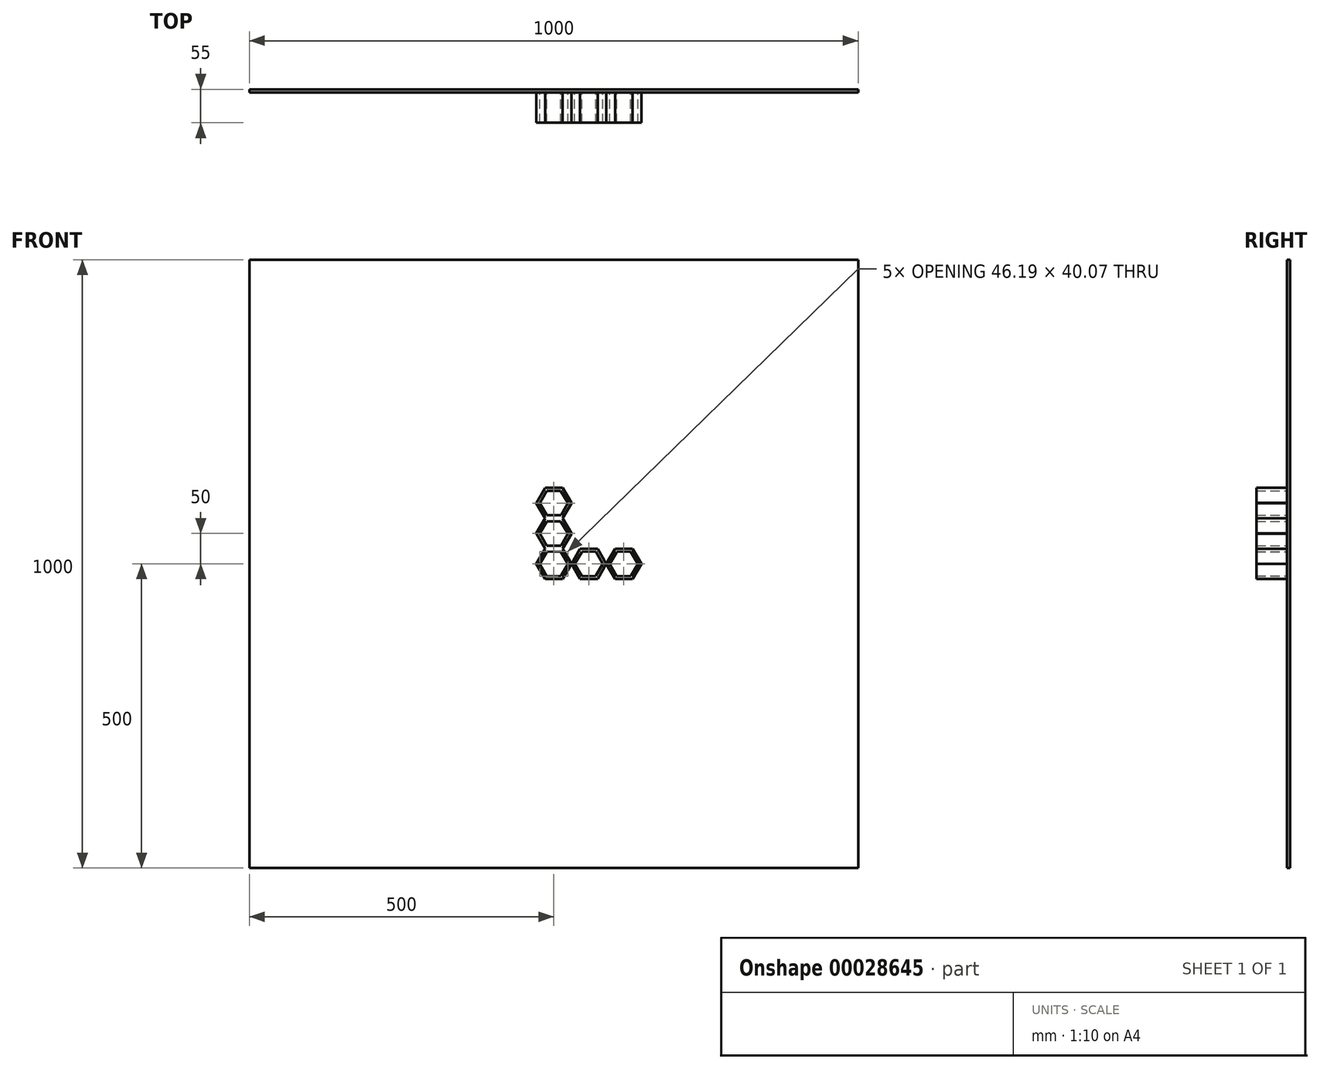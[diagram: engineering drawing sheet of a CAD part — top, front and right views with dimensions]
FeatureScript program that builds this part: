
annotation { "Feature Type Name" : "Feature", "Feature Type Description" : "" }
export const myFeature = defineFeature(function(context is Context, id is Id, definition is map)
    precondition{}
    {
        {
            var Q0;
            Q0=qCreatedBy(makeId("Front.planeOp"),FACE);
            var sketch = newSketch(context, id + "F0", { "sketchPlane" : qUnion([Q0])});
            skLineSegment(sketch, "E0.rect.bottom", {"start": v(500, 500) * mm, "end": v(-500, 500) * mm});
            skLineSegment(sketch, "E0.rect.top", {"start": v(500, -500) * mm, "end": v(-500, -500) * mm});
            skLineSegment(sketch, "E0.rect.left", {"start": v(500, 500) * mm, "end": v(500, -500) * mm});
            skLineSegment(sketch, "E0.rect.right", {"start": v(-500, 500) * mm, "end": v(-500, -500) * mm});
            skPoint(sketch, "E0.rect.middle", {"position": v(0, 0) * mm});
            skSolve(sketch);
        }
        {
            var Q0;
            Q0=makeQuery(id+"F0.imprint","IMPRINT",FACE,{"disambiguationData":[TD([[makeQuery(id+"F0.imprint","IMPRINT",EDGE,{"derivedFrom":sQuery(id+"F0.wireOp",EDGE,"E0.rect.bottom")}),1.0]])]});
            extrude(context, id + "F1", {"entities" : qUnion([Q0]), "depth" : 5 * mm});
        }
        {
            var Q0;
            Q0=makeQuery(id+"F1.opExtrude","CAP_FACE",FACE,{"disambiguationData":[OSD([sQuery(id+"F0.wireOp",EDGE,"E0.rect.bottom"),sQuery(id+"F0.wireOp",EDGE,"E0.rect.top"),sQuery(id+"F0.wireOp",EDGE,"E0.rect.left"),sQuery(id+"F0.wireOp",EDGE,"E0.rect.right")])],"isStart":false});
            var sketch = newSketch(context, id + "F2", { "sketchPlane" : qUnion([Q0])});
            skCircle(sketch, "E1.cCircle", {"center": v(0, 0) * mm, "radius": 25 * mm, "construction": true});
            skLineSegment(sketch, "E1.0", {"start": v(-14.43, 25) * mm, "end": v(14.43, 25) * mm});
            skLineSegment(sketch, "E1.1", {"start": v(14.43, 25) * mm, "end": v(28.87, 0) * mm});
            skLineSegment(sketch, "E1.2", {"start": v(28.87, 0) * mm, "end": v(14.43, -25) * mm});
            skLineSegment(sketch, "E1.3", {"start": v(14.43, -25) * mm, "end": v(-14.43, -25) * mm});
            skLineSegment(sketch, "E1.4", {"start": v(-14.43, -25) * mm, "end": v(-28.87, 0) * mm});
            skLineSegment(sketch, "E1.5", {"start": v(-28.87, 0) * mm, "end": v(-14.43, 25) * mm});
            skPoint(sketch, "E1.0.midPoint", {"position": v(0, 25) * mm});
            skCircle(sketch, "E2.cCircle", {"center": v(0, 0) * mm, "radius": 20 * mm, "construction": true});
            skLineSegment(sketch, "E2.0", {"start": v(11.49, 20.04) * mm, "end": v(23.1, 0.07) * mm});
            skLineSegment(sketch, "E2.1", {"start": v(23.1, 0.07) * mm, "end": v(11.6, -19.96) * mm});
            skLineSegment(sketch, "E2.2", {"start": v(11.6, -19.96) * mm, "end": v(-11.49, -20.04) * mm});
            skLineSegment(sketch, "E2.3", {"start": v(-11.49, -20.04) * mm, "end": v(-23.1, -0.07) * mm});
            skLineSegment(sketch, "E2.4", {"start": v(-23.1, -0.07) * mm, "end": v(-11.6, 19.96) * mm});
            skLineSegment(sketch, "E2.5", {"start": v(-11.6, 19.96) * mm, "end": v(11.49, 20.04) * mm});
            skPoint(sketch, "E2.0.midPoint", {"position": v(17.29, 10.05) * mm});
            skLineSegment(sketch, "E3.0.1.7", {"start": v(-14.43, 25) * mm, "end": v(-28.87, 50) * mm});
            skLineSegment(sketch, "E3.0.1.9", {"start": v(14.43, 25) * mm, "end": v(-14.43, 25) * mm});
            skLineSegment(sketch, "E3.0.1.10", {"start": v(28.87, 50) * mm, "end": v(14.43, 25) * mm});
            skPoint(sketch, "E3.0.1.12", {"position": v(0, 75) * mm});
            skPoint(sketch, "E3.0.1.13", {"position": v(17.29, 60.05) * mm});
            skLineSegment(sketch, "E3.0.1.16", {"start": v(11.6, 30.04) * mm, "end": v(-11.49, 29.96) * mm});
            skCircle(sketch, "E3.0.1.19", {"center": v(0, 50) * mm, "radius": 25 * mm, "construction": true});
            skLineSegment(sketch, "E3.0.1.20", {"start": v(-14.43, 75) * mm, "end": v(14.43, 75) * mm});
            skLineSegment(sketch, "E3.0.1.23", {"start": v(-11.6, 69.96) * mm, "end": v(11.49, 70.04) * mm});
            skLineSegment(sketch, "E3.0.1.28", {"start": v(-28.87, 50) * mm, "end": v(-14.43, 75) * mm});
            skLineSegment(sketch, "E3.0.1.31", {"start": v(14.43, 75) * mm, "end": v(28.87, 50) * mm});
            skCircle(sketch, "E3.0.1.36", {"center": v(0, 50) * mm, "radius": 20 * mm, "construction": true});
            skLineSegment(sketch, "E3.0.1.38", {"start": v(-23.1, 49.93) * mm, "end": v(-11.6, 69.96) * mm});
            skLineSegment(sketch, "E3.0.1.39", {"start": v(-11.49, 29.96) * mm, "end": v(-23.1, 49.93) * mm});
            skLineSegment(sketch, "E3.0.1.40", {"start": v(23.1, 50.07) * mm, "end": v(11.6, 30.04) * mm});
            skLineSegment(sketch, "E3.0.1.41", {"start": v(11.49, 70.04) * mm, "end": v(23.1, 50.07) * mm});
            skLineSegment(sketch, "E3.0.2.7", {"start": v(-14.43, 75) * mm, "end": v(-28.87, 100) * mm});
            skLineSegment(sketch, "E3.0.2.9", {"start": v(14.43, 75) * mm, "end": v(-14.43, 75) * mm});
            skLineSegment(sketch, "E3.0.2.10", {"start": v(28.87, 100) * mm, "end": v(14.43, 75) * mm});
            skPoint(sketch, "E3.0.2.12", {"position": v(0, 125) * mm});
            skPoint(sketch, "E3.0.2.13", {"position": v(17.29, 110.05) * mm});
            skLineSegment(sketch, "E3.0.2.16", {"start": v(11.6, 80.04) * mm, "end": v(-11.49, 79.96) * mm});
            skCircle(sketch, "E3.0.2.19", {"center": v(0, 100) * mm, "radius": 25 * mm, "construction": true});
            skLineSegment(sketch, "E3.0.2.20", {"start": v(-14.43, 125) * mm, "end": v(14.43, 125) * mm});
            skLineSegment(sketch, "E3.0.2.23", {"start": v(-11.6, 119.96) * mm, "end": v(11.49, 120.04) * mm});
            skLineSegment(sketch, "E3.0.2.28", {"start": v(-28.87, 100) * mm, "end": v(-14.43, 125) * mm});
            skLineSegment(sketch, "E3.0.2.31", {"start": v(14.43, 125) * mm, "end": v(28.87, 100) * mm});
            skCircle(sketch, "E3.0.2.36", {"center": v(0, 100) * mm, "radius": 20 * mm, "construction": true});
            skLineSegment(sketch, "E3.0.2.38", {"start": v(-23.1, 99.93) * mm, "end": v(-11.6, 119.96) * mm});
            skLineSegment(sketch, "E3.0.2.39", {"start": v(-11.49, 79.96) * mm, "end": v(-23.1, 99.93) * mm});
            skLineSegment(sketch, "E3.0.2.40", {"start": v(23.1, 100.07) * mm, "end": v(11.6, 80.04) * mm});
            skLineSegment(sketch, "E3.0.2.41", {"start": v(11.49, 120.04) * mm, "end": v(23.1, 100.07) * mm});
            skLineSegment(sketch, "E3.0.3.7", {"start": v(-14.43, 125) * mm, "end": v(-28.87, 150) * mm});
            skLineSegment(sketch, "E3.0.3.9", {"start": v(14.43, 125) * mm, "end": v(-14.43, 125) * mm});
            skLineSegment(sketch, "E3.0.3.10", {"start": v(28.87, 150) * mm, "end": v(14.43, 125) * mm});
            skPoint(sketch, "E3.0.3.12", {"position": v(0, 175) * mm});
            skPoint(sketch, "E3.0.3.13", {"position": v(17.29, 160.05) * mm});
            skLineSegment(sketch, "E3.0.3.16", {"start": v(11.6, 130.04) * mm, "end": v(-11.49, 129.96) * mm});
            skCircle(sketch, "E3.0.3.19", {"center": v(0, 150) * mm, "radius": 25 * mm, "construction": true});
            skLineSegment(sketch, "E3.0.3.20", {"start": v(-14.43, 175) * mm, "end": v(14.43, 175) * mm});
            skLineSegment(sketch, "E3.0.3.23", {"start": v(-11.6, 169.96) * mm, "end": v(11.49, 170.04) * mm});
            skLineSegment(sketch, "E3.0.3.28", {"start": v(-28.87, 150) * mm, "end": v(-14.43, 175) * mm});
            skLineSegment(sketch, "E3.0.3.31", {"start": v(14.43, 175) * mm, "end": v(28.87, 150) * mm});
            skCircle(sketch, "E3.0.3.36", {"center": v(0, 150) * mm, "radius": 20 * mm, "construction": true});
            skLineSegment(sketch, "E3.0.3.38", {"start": v(-23.1, 149.93) * mm, "end": v(-11.6, 169.96) * mm});
            skLineSegment(sketch, "E3.0.3.39", {"start": v(-11.49, 129.96) * mm, "end": v(-23.1, 149.93) * mm});
            skLineSegment(sketch, "E3.0.3.40", {"start": v(23.1, 150.07) * mm, "end": v(11.6, 130.04) * mm});
            skLineSegment(sketch, "E3.0.3.41", {"start": v(11.49, 170.04) * mm, "end": v(23.1, 150.07) * mm});
            skLineSegment(sketch, "E3.0.4.7", {"start": v(-14.43, 175) * mm, "end": v(-28.87, 200) * mm});
            skLineSegment(sketch, "E3.0.4.9", {"start": v(14.43, 175) * mm, "end": v(-14.43, 175) * mm});
            skLineSegment(sketch, "E3.0.4.10", {"start": v(28.87, 200) * mm, "end": v(14.43, 175) * mm});
            skPoint(sketch, "E3.0.4.12", {"position": v(0, 225) * mm});
            skPoint(sketch, "E3.0.4.13", {"position": v(17.29, 210.05) * mm});
            skLineSegment(sketch, "E3.0.4.16", {"start": v(11.6, 180.04) * mm, "end": v(-11.49, 179.96) * mm});
            skCircle(sketch, "E3.0.4.19", {"center": v(0, 200) * mm, "radius": 25 * mm, "construction": true});
            skLineSegment(sketch, "E3.0.4.20", {"start": v(-14.43, 225) * mm, "end": v(14.43, 225) * mm});
            skLineSegment(sketch, "E3.0.4.23", {"start": v(-11.6, 219.96) * mm, "end": v(11.49, 220.04) * mm});
            skLineSegment(sketch, "E3.0.4.28", {"start": v(-28.87, 200) * mm, "end": v(-14.43, 225) * mm});
            skLineSegment(sketch, "E3.0.4.31", {"start": v(14.43, 225) * mm, "end": v(28.87, 200) * mm});
            skCircle(sketch, "E3.0.4.36", {"center": v(0, 200) * mm, "radius": 20 * mm, "construction": true});
            skLineSegment(sketch, "E3.0.4.38", {"start": v(-23.1, 199.93) * mm, "end": v(-11.6, 219.96) * mm});
            skLineSegment(sketch, "E3.0.4.39", {"start": v(-11.49, 179.96) * mm, "end": v(-23.1, 199.93) * mm});
            skLineSegment(sketch, "E3.0.4.40", {"start": v(23.1, 200.07) * mm, "end": v(11.6, 180.04) * mm});
            skLineSegment(sketch, "E3.0.4.41", {"start": v(11.49, 220.04) * mm, "end": v(23.1, 200.07) * mm});
            skLineSegment(sketch, "E3.0.5.7", {"start": v(-14.43, 225) * mm, "end": v(-28.87, 250) * mm});
            skLineSegment(sketch, "E3.0.5.9", {"start": v(14.43, 225) * mm, "end": v(-14.43, 225) * mm});
            skLineSegment(sketch, "E3.0.5.10", {"start": v(28.87, 250) * mm, "end": v(14.43, 225) * mm});
            skPoint(sketch, "E3.0.5.12", {"position": v(0, 275) * mm});
            skPoint(sketch, "E3.0.5.13", {"position": v(17.29, 260.05) * mm});
            skLineSegment(sketch, "E3.0.5.16", {"start": v(11.6, 230.04) * mm, "end": v(-11.49, 229.96) * mm});
            skCircle(sketch, "E3.0.5.19", {"center": v(0, 250) * mm, "radius": 25 * mm, "construction": true});
            skLineSegment(sketch, "E3.0.5.20", {"start": v(-14.43, 275) * mm, "end": v(14.43, 275) * mm});
            skLineSegment(sketch, "E3.0.5.23", {"start": v(-11.6, 269.96) * mm, "end": v(11.49, 270.04) * mm});
            skLineSegment(sketch, "E3.0.5.28", {"start": v(-28.87, 250) * mm, "end": v(-14.43, 275) * mm});
            skLineSegment(sketch, "E3.0.5.31", {"start": v(14.43, 275) * mm, "end": v(28.87, 250) * mm});
            skCircle(sketch, "E3.0.5.36", {"center": v(0, 250) * mm, "radius": 20 * mm, "construction": true});
            skLineSegment(sketch, "E3.0.5.38", {"start": v(-23.1, 249.93) * mm, "end": v(-11.6, 269.96) * mm});
            skLineSegment(sketch, "E3.0.5.39", {"start": v(-11.49, 229.96) * mm, "end": v(-23.1, 249.93) * mm});
            skLineSegment(sketch, "E3.0.5.40", {"start": v(23.1, 250.07) * mm, "end": v(11.6, 230.04) * mm});
            skLineSegment(sketch, "E3.0.5.41", {"start": v(11.49, 270.04) * mm, "end": v(23.1, 250.07) * mm});
            skLineSegment(sketch, "E3.0.6.7", {"start": v(-14.43, 275) * mm, "end": v(-28.87, 300) * mm});
            skLineSegment(sketch, "E3.0.6.9", {"start": v(14.43, 275) * mm, "end": v(-14.43, 275) * mm});
            skLineSegment(sketch, "E3.0.6.10", {"start": v(28.87, 300) * mm, "end": v(14.43, 275) * mm});
            skPoint(sketch, "E3.0.6.12", {"position": v(0, 325) * mm});
            skPoint(sketch, "E3.0.6.13", {"position": v(17.29, 310.05) * mm});
            skLineSegment(sketch, "E3.0.6.16", {"start": v(11.6, 280.04) * mm, "end": v(-11.49, 279.96) * mm});
            skCircle(sketch, "E3.0.6.19", {"center": v(0, 300) * mm, "radius": 25 * mm, "construction": true});
            skLineSegment(sketch, "E3.0.6.20", {"start": v(-14.43, 325) * mm, "end": v(14.43, 325) * mm});
            skLineSegment(sketch, "E3.0.6.23", {"start": v(-11.6, 319.96) * mm, "end": v(11.49, 320.04) * mm});
            skLineSegment(sketch, "E3.0.6.28", {"start": v(-28.87, 300) * mm, "end": v(-14.43, 325) * mm});
            skLineSegment(sketch, "E3.0.6.31", {"start": v(14.43, 325) * mm, "end": v(28.87, 300) * mm});
            skCircle(sketch, "E3.0.6.36", {"center": v(0, 300) * mm, "radius": 20 * mm, "construction": true});
            skLineSegment(sketch, "E3.0.6.38", {"start": v(-23.1, 299.93) * mm, "end": v(-11.6, 319.96) * mm});
            skLineSegment(sketch, "E3.0.6.39", {"start": v(-11.49, 279.96) * mm, "end": v(-23.1, 299.93) * mm});
            skLineSegment(sketch, "E3.0.6.40", {"start": v(23.1, 300.07) * mm, "end": v(11.6, 280.04) * mm});
            skLineSegment(sketch, "E3.0.6.41", {"start": v(11.49, 320.04) * mm, "end": v(23.1, 300.07) * mm});
            skLineSegment(sketch, "E3.0.7.7", {"start": v(-14.43, 325) * mm, "end": v(-28.87, 350) * mm});
            skLineSegment(sketch, "E3.0.7.9", {"start": v(14.43, 325) * mm, "end": v(-14.43, 325) * mm});
            skLineSegment(sketch, "E3.0.7.10", {"start": v(28.87, 350) * mm, "end": v(14.43, 325) * mm});
            skPoint(sketch, "E3.0.7.12", {"position": v(0, 375) * mm});
            skPoint(sketch, "E3.0.7.13", {"position": v(17.29, 360.05) * mm});
            skLineSegment(sketch, "E3.0.7.16", {"start": v(11.6, 330.04) * mm, "end": v(-11.49, 329.96) * mm});
            skCircle(sketch, "E3.0.7.19", {"center": v(0, 350) * mm, "radius": 25 * mm, "construction": true});
            skLineSegment(sketch, "E3.0.7.20", {"start": v(-14.43, 375) * mm, "end": v(14.43, 375) * mm});
            skLineSegment(sketch, "E3.0.7.23", {"start": v(-11.6, 369.96) * mm, "end": v(11.49, 370.04) * mm});
            skLineSegment(sketch, "E3.0.7.28", {"start": v(-28.87, 350) * mm, "end": v(-14.43, 375) * mm});
            skLineSegment(sketch, "E3.0.7.31", {"start": v(14.43, 375) * mm, "end": v(28.87, 350) * mm});
            skCircle(sketch, "E3.0.7.36", {"center": v(0, 350) * mm, "radius": 20 * mm, "construction": true});
            skLineSegment(sketch, "E3.0.7.38", {"start": v(-23.1, 349.93) * mm, "end": v(-11.6, 369.96) * mm});
            skLineSegment(sketch, "E3.0.7.39", {"start": v(-11.49, 329.96) * mm, "end": v(-23.1, 349.93) * mm});
            skLineSegment(sketch, "E3.0.7.40", {"start": v(23.1, 350.07) * mm, "end": v(11.6, 330.04) * mm});
            skLineSegment(sketch, "E3.0.7.41", {"start": v(11.49, 370.04) * mm, "end": v(23.1, 350.07) * mm});
            skLineSegment(sketch, "E3.0.8.7", {"start": v(-14.43, 375) * mm, "end": v(-28.87, 400) * mm});
            skLineSegment(sketch, "E3.0.8.9", {"start": v(14.43, 375) * mm, "end": v(-14.43, 375) * mm});
            skLineSegment(sketch, "E3.0.8.10", {"start": v(28.87, 400) * mm, "end": v(14.43, 375) * mm});
            skPoint(sketch, "E3.0.8.12", {"position": v(0, 425) * mm});
            skPoint(sketch, "E3.0.8.13", {"position": v(17.29, 410.05) * mm});
            skLineSegment(sketch, "E3.0.8.16", {"start": v(11.6, 380.04) * mm, "end": v(-11.49, 379.96) * mm});
            skCircle(sketch, "E3.0.8.19", {"center": v(0, 400) * mm, "radius": 25 * mm, "construction": true});
            skLineSegment(sketch, "E3.0.8.20", {"start": v(-14.43, 425) * mm, "end": v(14.43, 425) * mm});
            skLineSegment(sketch, "E3.0.8.23", {"start": v(-11.6, 419.96) * mm, "end": v(11.49, 420.04) * mm});
            skLineSegment(sketch, "E3.0.8.28", {"start": v(-28.87, 400) * mm, "end": v(-14.43, 425) * mm});
            skLineSegment(sketch, "E3.0.8.31", {"start": v(14.43, 425) * mm, "end": v(28.87, 400) * mm});
            skCircle(sketch, "E3.0.8.36", {"center": v(0, 400) * mm, "radius": 20 * mm, "construction": true});
            skLineSegment(sketch, "E3.0.8.38", {"start": v(-23.1, 399.93) * mm, "end": v(-11.6, 419.96) * mm});
            skLineSegment(sketch, "E3.0.8.39", {"start": v(-11.49, 379.96) * mm, "end": v(-23.1, 399.93) * mm});
            skLineSegment(sketch, "E3.0.8.40", {"start": v(23.1, 400.07) * mm, "end": v(11.6, 380.04) * mm});
            skLineSegment(sketch, "E3.0.8.41", {"start": v(11.49, 420.04) * mm, "end": v(23.1, 400.07) * mm});
            skLineSegment(sketch, "E3.0.9.7", {"start": v(-14.43, 425) * mm, "end": v(-28.87, 450) * mm});
            skLineSegment(sketch, "E3.0.9.9", {"start": v(14.43, 425) * mm, "end": v(-14.43, 425) * mm});
            skLineSegment(sketch, "E3.0.9.10", {"start": v(28.87, 450) * mm, "end": v(14.43, 425) * mm});
            skPoint(sketch, "E3.0.9.12", {"position": v(0, 475) * mm});
            skPoint(sketch, "E3.0.9.13", {"position": v(17.29, 460.05) * mm});
            skLineSegment(sketch, "E3.0.9.16", {"start": v(11.6, 430.04) * mm, "end": v(-11.49, 429.96) * mm});
            skCircle(sketch, "E3.0.9.19", {"center": v(0, 450) * mm, "radius": 25 * mm, "construction": true});
            skLineSegment(sketch, "E3.0.9.20", {"start": v(-14.43, 475) * mm, "end": v(14.43, 475) * mm});
            skLineSegment(sketch, "E3.0.9.23", {"start": v(-11.6, 469.96) * mm, "end": v(11.49, 470.04) * mm});
            skLineSegment(sketch, "E3.0.9.28", {"start": v(-28.87, 450) * mm, "end": v(-14.43, 475) * mm});
            skLineSegment(sketch, "E3.0.9.31", {"start": v(14.43, 475) * mm, "end": v(28.87, 450) * mm});
            skCircle(sketch, "E3.0.9.36", {"center": v(0, 450) * mm, "radius": 20 * mm, "construction": true});
            skLineSegment(sketch, "E3.0.9.38", {"start": v(-23.1, 449.93) * mm, "end": v(-11.6, 469.96) * mm});
            skLineSegment(sketch, "E3.0.9.39", {"start": v(-11.49, 429.96) * mm, "end": v(-23.1, 449.93) * mm});
            skLineSegment(sketch, "E3.0.9.40", {"start": v(23.1, 450.07) * mm, "end": v(11.6, 430.04) * mm});
            skLineSegment(sketch, "E3.0.9.41", {"start": v(11.49, 470.04) * mm, "end": v(23.1, 450.07) * mm});
            skLineSegment(sketch, "E3.1.0.7", {"start": v(43.07, -25) * mm, "end": v(28.63, 0) * mm});
            skLineSegment(sketch, "E3.1.0.9", {"start": v(71.93, -25) * mm, "end": v(43.07, -25) * mm});
            skLineSegment(sketch, "E3.1.0.10", {"start": v(86.37, 0) * mm, "end": v(71.93, -25) * mm});
            skPoint(sketch, "E3.1.0.12", {"position": v(57.5, 25) * mm});
            skPoint(sketch, "E3.1.0.13", {"position": v(74.79, 10.05) * mm});
            skLineSegment(sketch, "E3.1.0.16", {"start": v(69.1, -19.96) * mm, "end": v(46.01, -20.04) * mm});
            skCircle(sketch, "E3.1.0.19", {"center": v(57.5, 0) * mm, "radius": 25 * mm, "construction": true});
            skLineSegment(sketch, "E3.1.0.20", {"start": v(43.07, 25) * mm, "end": v(71.93, 25) * mm});
            skLineSegment(sketch, "E3.1.0.23", {"start": v(45.9, 19.96) * mm, "end": v(68.99, 20.04) * mm});
            skLineSegment(sketch, "E3.1.0.28", {"start": v(28.63, 0) * mm, "end": v(43.07, 25) * mm});
            skLineSegment(sketch, "E3.1.0.31", {"start": v(71.93, 25) * mm, "end": v(86.37, 0) * mm});
            skCircle(sketch, "E3.1.0.36", {"center": v(57.5, 0) * mm, "radius": 20 * mm, "construction": true});
            skLineSegment(sketch, "E3.1.0.38", {"start": v(34.4, -0.07) * mm, "end": v(45.9, 19.96) * mm});
            skLineSegment(sketch, "E3.1.0.39", {"start": v(46.01, -20.04) * mm, "end": v(34.4, -0.07) * mm});
            skLineSegment(sketch, "E3.1.0.40", {"start": v(80.6, 0.07) * mm, "end": v(69.1, -19.96) * mm});
            skLineSegment(sketch, "E3.1.0.41", {"start": v(68.99, 20.04) * mm, "end": v(80.6, 0.07) * mm});
            skLineSegment(sketch, "E3.1.1.7", {"start": v(43.07, 25) * mm, "end": v(28.63, 50) * mm});
            skLineSegment(sketch, "E3.1.1.9", {"start": v(71.93, 25) * mm, "end": v(43.07, 25) * mm});
            skLineSegment(sketch, "E3.1.1.10", {"start": v(86.37, 50) * mm, "end": v(71.93, 25) * mm});
            skPoint(sketch, "E3.1.1.12", {"position": v(57.5, 75) * mm});
            skPoint(sketch, "E3.1.1.13", {"position": v(74.79, 60.05) * mm});
            skLineSegment(sketch, "E3.1.1.16", {"start": v(69.1, 30.04) * mm, "end": v(46.01, 29.96) * mm});
            skCircle(sketch, "E3.1.1.19", {"center": v(57.5, 50) * mm, "radius": 25 * mm, "construction": true});
            skLineSegment(sketch, "E3.1.1.20", {"start": v(43.07, 75) * mm, "end": v(71.93, 75) * mm});
            skLineSegment(sketch, "E3.1.1.23", {"start": v(45.9, 69.96) * mm, "end": v(68.99, 70.04) * mm});
            skLineSegment(sketch, "E3.1.1.28", {"start": v(28.63, 50) * mm, "end": v(43.07, 75) * mm});
            skLineSegment(sketch, "E3.1.1.31", {"start": v(71.93, 75) * mm, "end": v(86.37, 50) * mm});
            skCircle(sketch, "E3.1.1.36", {"center": v(57.5, 50) * mm, "radius": 20 * mm, "construction": true});
            skLineSegment(sketch, "E3.1.1.38", {"start": v(34.4, 49.93) * mm, "end": v(45.9, 69.96) * mm});
            skLineSegment(sketch, "E3.1.1.39", {"start": v(46.01, 29.96) * mm, "end": v(34.4, 49.93) * mm});
            skLineSegment(sketch, "E3.1.1.40", {"start": v(80.6, 50.07) * mm, "end": v(69.1, 30.04) * mm});
            skLineSegment(sketch, "E3.1.1.41", {"start": v(68.99, 70.04) * mm, "end": v(80.6, 50.07) * mm});
            skLineSegment(sketch, "E3.1.2.7", {"start": v(43.07, 75) * mm, "end": v(28.63, 100) * mm});
            skLineSegment(sketch, "E3.1.2.9", {"start": v(71.93, 75) * mm, "end": v(43.07, 75) * mm});
            skLineSegment(sketch, "E3.1.2.10", {"start": v(86.37, 100) * mm, "end": v(71.93, 75) * mm});
            skPoint(sketch, "E3.1.2.12", {"position": v(57.5, 125) * mm});
            skPoint(sketch, "E3.1.2.13", {"position": v(74.79, 110.05) * mm});
            skLineSegment(sketch, "E3.1.2.16", {"start": v(69.1, 80.04) * mm, "end": v(46.01, 79.96) * mm});
            skCircle(sketch, "E3.1.2.19", {"center": v(57.5, 100) * mm, "radius": 25 * mm, "construction": true});
            skLineSegment(sketch, "E3.1.2.20", {"start": v(43.07, 125) * mm, "end": v(71.93, 125) * mm});
            skLineSegment(sketch, "E3.1.2.23", {"start": v(45.9, 119.96) * mm, "end": v(68.99, 120.04) * mm});
            skLineSegment(sketch, "E3.1.2.28", {"start": v(28.63, 100) * mm, "end": v(43.07, 125) * mm});
            skLineSegment(sketch, "E3.1.2.31", {"start": v(71.93, 125) * mm, "end": v(86.37, 100) * mm});
            skCircle(sketch, "E3.1.2.36", {"center": v(57.5, 100) * mm, "radius": 20 * mm, "construction": true});
            skLineSegment(sketch, "E3.1.2.38", {"start": v(34.4, 99.93) * mm, "end": v(45.9, 119.96) * mm});
            skLineSegment(sketch, "E3.1.2.39", {"start": v(46.01, 79.96) * mm, "end": v(34.4, 99.93) * mm});
            skLineSegment(sketch, "E3.1.2.40", {"start": v(80.6, 100.07) * mm, "end": v(69.1, 80.04) * mm});
            skLineSegment(sketch, "E3.1.2.41", {"start": v(68.99, 120.04) * mm, "end": v(80.6, 100.07) * mm});
            skLineSegment(sketch, "E3.1.3.7", {"start": v(43.07, 125) * mm, "end": v(28.63, 150) * mm});
            skLineSegment(sketch, "E3.1.3.9", {"start": v(71.93, 125) * mm, "end": v(43.07, 125) * mm});
            skLineSegment(sketch, "E3.1.3.10", {"start": v(86.37, 150) * mm, "end": v(71.93, 125) * mm});
            skPoint(sketch, "E3.1.3.12", {"position": v(57.5, 175) * mm});
            skPoint(sketch, "E3.1.3.13", {"position": v(74.79, 160.05) * mm});
            skLineSegment(sketch, "E3.1.3.16", {"start": v(69.1, 130.04) * mm, "end": v(46.01, 129.96) * mm});
            skCircle(sketch, "E3.1.3.19", {"center": v(57.5, 150) * mm, "radius": 25 * mm, "construction": true});
            skLineSegment(sketch, "E3.1.3.20", {"start": v(43.07, 175) * mm, "end": v(71.93, 175) * mm});
            skLineSegment(sketch, "E3.1.3.23", {"start": v(45.9, 169.96) * mm, "end": v(68.99, 170.04) * mm});
            skLineSegment(sketch, "E3.1.3.28", {"start": v(28.63, 150) * mm, "end": v(43.07, 175) * mm});
            skLineSegment(sketch, "E3.1.3.31", {"start": v(71.93, 175) * mm, "end": v(86.37, 150) * mm});
            skCircle(sketch, "E3.1.3.36", {"center": v(57.5, 150) * mm, "radius": 20 * mm, "construction": true});
            skLineSegment(sketch, "E3.1.3.38", {"start": v(34.4, 149.93) * mm, "end": v(45.9, 169.96) * mm});
            skLineSegment(sketch, "E3.1.3.39", {"start": v(46.01, 129.96) * mm, "end": v(34.4, 149.93) * mm});
            skLineSegment(sketch, "E3.1.3.40", {"start": v(80.6, 150.07) * mm, "end": v(69.1, 130.04) * mm});
            skLineSegment(sketch, "E3.1.3.41", {"start": v(68.99, 170.04) * mm, "end": v(80.6, 150.07) * mm});
            skLineSegment(sketch, "E3.1.4.7", {"start": v(43.07, 175) * mm, "end": v(28.63, 200) * mm});
            skLineSegment(sketch, "E3.1.4.9", {"start": v(71.93, 175) * mm, "end": v(43.07, 175) * mm});
            skLineSegment(sketch, "E3.1.4.10", {"start": v(86.37, 200) * mm, "end": v(71.93, 175) * mm});
            skPoint(sketch, "E3.1.4.12", {"position": v(57.5, 225) * mm});
            skPoint(sketch, "E3.1.4.13", {"position": v(74.79, 210.05) * mm});
            skLineSegment(sketch, "E3.1.4.16", {"start": v(69.1, 180.04) * mm, "end": v(46.01, 179.96) * mm});
            skCircle(sketch, "E3.1.4.19", {"center": v(57.5, 200) * mm, "radius": 25 * mm, "construction": true});
            skLineSegment(sketch, "E3.1.4.20", {"start": v(43.07, 225) * mm, "end": v(71.93, 225) * mm});
            skLineSegment(sketch, "E3.1.4.23", {"start": v(45.9, 219.96) * mm, "end": v(68.99, 220.04) * mm});
            skLineSegment(sketch, "E3.1.4.28", {"start": v(28.63, 200) * mm, "end": v(43.07, 225) * mm});
            skLineSegment(sketch, "E3.1.4.31", {"start": v(71.93, 225) * mm, "end": v(86.37, 200) * mm});
            skCircle(sketch, "E3.1.4.36", {"center": v(57.5, 200) * mm, "radius": 20 * mm, "construction": true});
            skLineSegment(sketch, "E3.1.4.38", {"start": v(34.4, 199.93) * mm, "end": v(45.9, 219.96) * mm});
            skLineSegment(sketch, "E3.1.4.39", {"start": v(46.01, 179.96) * mm, "end": v(34.4, 199.93) * mm});
            skLineSegment(sketch, "E3.1.4.40", {"start": v(80.6, 200.07) * mm, "end": v(69.1, 180.04) * mm});
            skLineSegment(sketch, "E3.1.4.41", {"start": v(68.99, 220.04) * mm, "end": v(80.6, 200.07) * mm});
            skLineSegment(sketch, "E3.1.5.7", {"start": v(43.07, 225) * mm, "end": v(28.63, 250) * mm});
            skLineSegment(sketch, "E3.1.5.9", {"start": v(71.93, 225) * mm, "end": v(43.07, 225) * mm});
            skLineSegment(sketch, "E3.1.5.10", {"start": v(86.37, 250) * mm, "end": v(71.93, 225) * mm});
            skPoint(sketch, "E3.1.5.12", {"position": v(57.5, 275) * mm});
            skPoint(sketch, "E3.1.5.13", {"position": v(74.79, 260.05) * mm});
            skLineSegment(sketch, "E3.1.5.16", {"start": v(69.1, 230.04) * mm, "end": v(46.01, 229.96) * mm});
            skCircle(sketch, "E3.1.5.19", {"center": v(57.5, 250) * mm, "radius": 25 * mm, "construction": true});
            skLineSegment(sketch, "E3.1.5.20", {"start": v(43.07, 275) * mm, "end": v(71.93, 275) * mm});
            skLineSegment(sketch, "E3.1.5.23", {"start": v(45.9, 269.96) * mm, "end": v(68.99, 270.04) * mm});
            skLineSegment(sketch, "E3.1.5.28", {"start": v(28.63, 250) * mm, "end": v(43.07, 275) * mm});
            skLineSegment(sketch, "E3.1.5.31", {"start": v(71.93, 275) * mm, "end": v(86.37, 250) * mm});
            skCircle(sketch, "E3.1.5.36", {"center": v(57.5, 250) * mm, "radius": 20 * mm, "construction": true});
            skLineSegment(sketch, "E3.1.5.38", {"start": v(34.4, 249.93) * mm, "end": v(45.9, 269.96) * mm});
            skLineSegment(sketch, "E3.1.5.39", {"start": v(46.01, 229.96) * mm, "end": v(34.4, 249.93) * mm});
            skLineSegment(sketch, "E3.1.5.40", {"start": v(80.6, 250.07) * mm, "end": v(69.1, 230.04) * mm});
            skLineSegment(sketch, "E3.1.5.41", {"start": v(68.99, 270.04) * mm, "end": v(80.6, 250.07) * mm});
            skLineSegment(sketch, "E3.1.6.7", {"start": v(43.07, 275) * mm, "end": v(28.63, 300) * mm});
            skLineSegment(sketch, "E3.1.6.9", {"start": v(71.93, 275) * mm, "end": v(43.07, 275) * mm});
            skLineSegment(sketch, "E3.1.6.10", {"start": v(86.37, 300) * mm, "end": v(71.93, 275) * mm});
            skPoint(sketch, "E3.1.6.12", {"position": v(57.5, 325) * mm});
            skPoint(sketch, "E3.1.6.13", {"position": v(74.79, 310.05) * mm});
            skLineSegment(sketch, "E3.1.6.16", {"start": v(69.1, 280.04) * mm, "end": v(46.01, 279.96) * mm});
            skCircle(sketch, "E3.1.6.19", {"center": v(57.5, 300) * mm, "radius": 25 * mm, "construction": true});
            skLineSegment(sketch, "E3.1.6.20", {"start": v(43.07, 325) * mm, "end": v(71.93, 325) * mm});
            skLineSegment(sketch, "E3.1.6.23", {"start": v(45.9, 319.96) * mm, "end": v(68.99, 320.04) * mm});
            skLineSegment(sketch, "E3.1.6.28", {"start": v(28.63, 300) * mm, "end": v(43.07, 325) * mm});
            skLineSegment(sketch, "E3.1.6.31", {"start": v(71.93, 325) * mm, "end": v(86.37, 300) * mm});
            skCircle(sketch, "E3.1.6.36", {"center": v(57.5, 300) * mm, "radius": 20 * mm, "construction": true});
            skLineSegment(sketch, "E3.1.6.38", {"start": v(34.4, 299.93) * mm, "end": v(45.9, 319.96) * mm});
            skLineSegment(sketch, "E3.1.6.39", {"start": v(46.01, 279.96) * mm, "end": v(34.4, 299.93) * mm});
            skLineSegment(sketch, "E3.1.6.40", {"start": v(80.6, 300.07) * mm, "end": v(69.1, 280.04) * mm});
            skLineSegment(sketch, "E3.1.6.41", {"start": v(68.99, 320.04) * mm, "end": v(80.6, 300.07) * mm});
            skLineSegment(sketch, "E3.1.7.7", {"start": v(43.07, 325) * mm, "end": v(28.63, 350) * mm});
            skLineSegment(sketch, "E3.1.7.9", {"start": v(71.93, 325) * mm, "end": v(43.07, 325) * mm});
            skLineSegment(sketch, "E3.1.7.10", {"start": v(86.37, 350) * mm, "end": v(71.93, 325) * mm});
            skPoint(sketch, "E3.1.7.12", {"position": v(57.5, 375) * mm});
            skPoint(sketch, "E3.1.7.13", {"position": v(74.79, 360.05) * mm});
            skLineSegment(sketch, "E3.1.7.16", {"start": v(69.1, 330.04) * mm, "end": v(46.01, 329.96) * mm});
            skCircle(sketch, "E3.1.7.19", {"center": v(57.5, 350) * mm, "radius": 25 * mm, "construction": true});
            skLineSegment(sketch, "E3.1.7.20", {"start": v(43.07, 375) * mm, "end": v(71.93, 375) * mm});
            skLineSegment(sketch, "E3.1.7.23", {"start": v(45.9, 369.96) * mm, "end": v(68.99, 370.04) * mm});
            skLineSegment(sketch, "E3.1.7.28", {"start": v(28.63, 350) * mm, "end": v(43.07, 375) * mm});
            skLineSegment(sketch, "E3.1.7.31", {"start": v(71.93, 375) * mm, "end": v(86.37, 350) * mm});
            skCircle(sketch, "E3.1.7.36", {"center": v(57.5, 350) * mm, "radius": 20 * mm, "construction": true});
            skLineSegment(sketch, "E3.1.7.38", {"start": v(34.4, 349.93) * mm, "end": v(45.9, 369.96) * mm});
            skLineSegment(sketch, "E3.1.7.39", {"start": v(46.01, 329.96) * mm, "end": v(34.4, 349.93) * mm});
            skLineSegment(sketch, "E3.1.7.40", {"start": v(80.6, 350.07) * mm, "end": v(69.1, 330.04) * mm});
            skLineSegment(sketch, "E3.1.7.41", {"start": v(68.99, 370.04) * mm, "end": v(80.6, 350.07) * mm});
            skLineSegment(sketch, "E3.1.8.7", {"start": v(43.07, 375) * mm, "end": v(28.63, 400) * mm});
            skLineSegment(sketch, "E3.1.8.9", {"start": v(71.93, 375) * mm, "end": v(43.07, 375) * mm});
            skLineSegment(sketch, "E3.1.8.10", {"start": v(86.37, 400) * mm, "end": v(71.93, 375) * mm});
            skPoint(sketch, "E3.1.8.12", {"position": v(57.5, 425) * mm});
            skPoint(sketch, "E3.1.8.13", {"position": v(74.79, 410.05) * mm});
            skLineSegment(sketch, "E3.1.8.16", {"start": v(69.1, 380.04) * mm, "end": v(46.01, 379.96) * mm});
            skCircle(sketch, "E3.1.8.19", {"center": v(57.5, 400) * mm, "radius": 25 * mm, "construction": true});
            skLineSegment(sketch, "E3.1.8.20", {"start": v(43.07, 425) * mm, "end": v(71.93, 425) * mm});
            skLineSegment(sketch, "E3.1.8.23", {"start": v(45.9, 419.96) * mm, "end": v(68.99, 420.04) * mm});
            skLineSegment(sketch, "E3.1.8.28", {"start": v(28.63, 400) * mm, "end": v(43.07, 425) * mm});
            skLineSegment(sketch, "E3.1.8.31", {"start": v(71.93, 425) * mm, "end": v(86.37, 400) * mm});
            skCircle(sketch, "E3.1.8.36", {"center": v(57.5, 400) * mm, "radius": 20 * mm, "construction": true});
            skLineSegment(sketch, "E3.1.8.38", {"start": v(34.4, 399.93) * mm, "end": v(45.9, 419.96) * mm});
            skLineSegment(sketch, "E3.1.8.39", {"start": v(46.01, 379.96) * mm, "end": v(34.4, 399.93) * mm});
            skLineSegment(sketch, "E3.1.8.40", {"start": v(80.6, 400.07) * mm, "end": v(69.1, 380.04) * mm});
            skLineSegment(sketch, "E3.1.8.41", {"start": v(68.99, 420.04) * mm, "end": v(80.6, 400.07) * mm});
            skLineSegment(sketch, "E3.1.9.7", {"start": v(43.07, 425) * mm, "end": v(28.63, 450) * mm});
            skLineSegment(sketch, "E3.1.9.9", {"start": v(71.93, 425) * mm, "end": v(43.07, 425) * mm});
            skLineSegment(sketch, "E3.1.9.10", {"start": v(86.37, 450) * mm, "end": v(71.93, 425) * mm});
            skPoint(sketch, "E3.1.9.12", {"position": v(57.5, 475) * mm});
            skPoint(sketch, "E3.1.9.13", {"position": v(74.79, 460.05) * mm});
            skLineSegment(sketch, "E3.1.9.16", {"start": v(69.1, 430.04) * mm, "end": v(46.01, 429.96) * mm});
            skCircle(sketch, "E3.1.9.19", {"center": v(57.5, 450) * mm, "radius": 25 * mm, "construction": true});
            skLineSegment(sketch, "E3.1.9.20", {"start": v(43.07, 475) * mm, "end": v(71.93, 475) * mm});
            skLineSegment(sketch, "E3.1.9.23", {"start": v(45.9, 469.96) * mm, "end": v(68.99, 470.04) * mm});
            skLineSegment(sketch, "E3.1.9.28", {"start": v(28.63, 450) * mm, "end": v(43.07, 475) * mm});
            skLineSegment(sketch, "E3.1.9.31", {"start": v(71.93, 475) * mm, "end": v(86.37, 450) * mm});
            skCircle(sketch, "E3.1.9.36", {"center": v(57.5, 450) * mm, "radius": 20 * mm, "construction": true});
            skLineSegment(sketch, "E3.1.9.38", {"start": v(34.4, 449.93) * mm, "end": v(45.9, 469.96) * mm});
            skLineSegment(sketch, "E3.1.9.39", {"start": v(46.01, 429.96) * mm, "end": v(34.4, 449.93) * mm});
            skLineSegment(sketch, "E3.1.9.40", {"start": v(80.6, 450.07) * mm, "end": v(69.1, 430.04) * mm});
            skLineSegment(sketch, "E3.1.9.41", {"start": v(68.99, 470.04) * mm, "end": v(80.6, 450.07) * mm});
            skLineSegment(sketch, "E3.2.0.7", {"start": v(100.57, -25) * mm, "end": v(86.13, 0) * mm});
            skLineSegment(sketch, "E3.2.0.9", {"start": v(129.43, -25) * mm, "end": v(100.57, -25) * mm});
            skLineSegment(sketch, "E3.2.0.10", {"start": v(143.87, 0) * mm, "end": v(129.43, -25) * mm});
            skPoint(sketch, "E3.2.0.12", {"position": v(115, 25) * mm});
            skPoint(sketch, "E3.2.0.13", {"position": v(132.29, 10.05) * mm});
            skLineSegment(sketch, "E3.2.0.16", {"start": v(126.6, -19.96) * mm, "end": v(103.51, -20.04) * mm});
            skCircle(sketch, "E3.2.0.19", {"center": v(115, 0) * mm, "radius": 25 * mm, "construction": true});
            skLineSegment(sketch, "E3.2.0.20", {"start": v(100.57, 25) * mm, "end": v(129.43, 25) * mm});
            skLineSegment(sketch, "E3.2.0.23", {"start": v(103.4, 19.96) * mm, "end": v(126.49, 20.04) * mm});
            skLineSegment(sketch, "E3.2.0.28", {"start": v(86.13, 0) * mm, "end": v(100.57, 25) * mm});
            skLineSegment(sketch, "E3.2.0.31", {"start": v(129.43, 25) * mm, "end": v(143.87, 0) * mm});
            skCircle(sketch, "E3.2.0.36", {"center": v(115, 0) * mm, "radius": 20 * mm, "construction": true});
            skLineSegment(sketch, "E3.2.0.38", {"start": v(91.9, -0.07) * mm, "end": v(103.4, 19.96) * mm});
            skLineSegment(sketch, "E3.2.0.39", {"start": v(103.51, -20.04) * mm, "end": v(91.9, -0.07) * mm});
            skLineSegment(sketch, "E3.2.0.40", {"start": v(138.1, 0.07) * mm, "end": v(126.6, -19.96) * mm});
            skLineSegment(sketch, "E3.2.0.41", {"start": v(126.49, 20.04) * mm, "end": v(138.1, 0.07) * mm});
            skLineSegment(sketch, "E3.2.1.7", {"start": v(100.57, 25) * mm, "end": v(86.13, 50) * mm});
            skLineSegment(sketch, "E3.2.1.9", {"start": v(129.43, 25) * mm, "end": v(100.57, 25) * mm});
            skLineSegment(sketch, "E3.2.1.10", {"start": v(143.87, 50) * mm, "end": v(129.43, 25) * mm});
            skPoint(sketch, "E3.2.1.12", {"position": v(115, 75) * mm});
            skPoint(sketch, "E3.2.1.13", {"position": v(132.29, 60.05) * mm});
            skLineSegment(sketch, "E3.2.1.16", {"start": v(126.6, 30.04) * mm, "end": v(103.51, 29.96) * mm});
            skCircle(sketch, "E3.2.1.19", {"center": v(115, 50) * mm, "radius": 25 * mm, "construction": true});
            skLineSegment(sketch, "E3.2.1.20", {"start": v(100.57, 75) * mm, "end": v(129.43, 75) * mm});
            skLineSegment(sketch, "E3.2.1.23", {"start": v(103.4, 69.96) * mm, "end": v(126.49, 70.04) * mm});
            skLineSegment(sketch, "E3.2.1.28", {"start": v(86.13, 50) * mm, "end": v(100.57, 75) * mm});
            skLineSegment(sketch, "E3.2.1.31", {"start": v(129.43, 75) * mm, "end": v(143.87, 50) * mm});
            skCircle(sketch, "E3.2.1.36", {"center": v(115, 50) * mm, "radius": 20 * mm, "construction": true});
            skLineSegment(sketch, "E3.2.1.38", {"start": v(91.9, 49.93) * mm, "end": v(103.4, 69.96) * mm});
            skLineSegment(sketch, "E3.2.1.39", {"start": v(103.51, 29.96) * mm, "end": v(91.9, 49.93) * mm});
            skLineSegment(sketch, "E3.2.1.40", {"start": v(138.1, 50.07) * mm, "end": v(126.6, 30.04) * mm});
            skLineSegment(sketch, "E3.2.1.41", {"start": v(126.49, 70.04) * mm, "end": v(138.1, 50.07) * mm});
            skLineSegment(sketch, "E3.2.2.7", {"start": v(100.57, 75) * mm, "end": v(86.13, 100) * mm});
            skLineSegment(sketch, "E3.2.2.9", {"start": v(129.43, 75) * mm, "end": v(100.57, 75) * mm});
            skLineSegment(sketch, "E3.2.2.10", {"start": v(143.87, 100) * mm, "end": v(129.43, 75) * mm});
            skPoint(sketch, "E3.2.2.12", {"position": v(115, 125) * mm});
            skPoint(sketch, "E3.2.2.13", {"position": v(132.29, 110.05) * mm});
            skLineSegment(sketch, "E3.2.2.16", {"start": v(126.6, 80.04) * mm, "end": v(103.51, 79.96) * mm});
            skCircle(sketch, "E3.2.2.19", {"center": v(115, 100) * mm, "radius": 25 * mm, "construction": true});
            skLineSegment(sketch, "E3.2.2.20", {"start": v(100.57, 125) * mm, "end": v(129.43, 125) * mm});
            skLineSegment(sketch, "E3.2.2.23", {"start": v(103.4, 119.96) * mm, "end": v(126.49, 120.04) * mm});
            skLineSegment(sketch, "E3.2.2.28", {"start": v(86.13, 100) * mm, "end": v(100.57, 125) * mm});
            skLineSegment(sketch, "E3.2.2.31", {"start": v(129.43, 125) * mm, "end": v(143.87, 100) * mm});
            skCircle(sketch, "E3.2.2.36", {"center": v(115, 100) * mm, "radius": 20 * mm, "construction": true});
            skLineSegment(sketch, "E3.2.2.38", {"start": v(91.9, 99.93) * mm, "end": v(103.4, 119.96) * mm});
            skLineSegment(sketch, "E3.2.2.39", {"start": v(103.51, 79.96) * mm, "end": v(91.9, 99.93) * mm});
            skLineSegment(sketch, "E3.2.2.40", {"start": v(138.1, 100.07) * mm, "end": v(126.6, 80.04) * mm});
            skLineSegment(sketch, "E3.2.2.41", {"start": v(126.49, 120.04) * mm, "end": v(138.1, 100.07) * mm});
            skLineSegment(sketch, "E3.2.3.7", {"start": v(100.57, 125) * mm, "end": v(86.13, 150) * mm});
            skLineSegment(sketch, "E3.2.3.9", {"start": v(129.43, 125) * mm, "end": v(100.57, 125) * mm});
            skLineSegment(sketch, "E3.2.3.10", {"start": v(143.87, 150) * mm, "end": v(129.43, 125) * mm});
            skPoint(sketch, "E3.2.3.12", {"position": v(115, 175) * mm});
            skPoint(sketch, "E3.2.3.13", {"position": v(132.29, 160.05) * mm});
            skLineSegment(sketch, "E3.2.3.16", {"start": v(126.6, 130.04) * mm, "end": v(103.51, 129.96) * mm});
            skCircle(sketch, "E3.2.3.19", {"center": v(115, 150) * mm, "radius": 25 * mm, "construction": true});
            skLineSegment(sketch, "E3.2.3.20", {"start": v(100.57, 175) * mm, "end": v(129.43, 175) * mm});
            skLineSegment(sketch, "E3.2.3.23", {"start": v(103.4, 169.96) * mm, "end": v(126.49, 170.04) * mm});
            skLineSegment(sketch, "E3.2.3.28", {"start": v(86.13, 150) * mm, "end": v(100.57, 175) * mm});
            skLineSegment(sketch, "E3.2.3.31", {"start": v(129.43, 175) * mm, "end": v(143.87, 150) * mm});
            skCircle(sketch, "E3.2.3.36", {"center": v(115, 150) * mm, "radius": 20 * mm, "construction": true});
            skLineSegment(sketch, "E3.2.3.38", {"start": v(91.9, 149.93) * mm, "end": v(103.4, 169.96) * mm});
            skLineSegment(sketch, "E3.2.3.39", {"start": v(103.51, 129.96) * mm, "end": v(91.9, 149.93) * mm});
            skLineSegment(sketch, "E3.2.3.40", {"start": v(138.1, 150.07) * mm, "end": v(126.6, 130.04) * mm});
            skLineSegment(sketch, "E3.2.3.41", {"start": v(126.49, 170.04) * mm, "end": v(138.1, 150.07) * mm});
            skLineSegment(sketch, "E3.2.4.7", {"start": v(100.57, 175) * mm, "end": v(86.13, 200) * mm});
            skLineSegment(sketch, "E3.2.4.9", {"start": v(129.43, 175) * mm, "end": v(100.57, 175) * mm});
            skLineSegment(sketch, "E3.2.4.10", {"start": v(143.87, 200) * mm, "end": v(129.43, 175) * mm});
            skPoint(sketch, "E3.2.4.12", {"position": v(115, 225) * mm});
            skPoint(sketch, "E3.2.4.13", {"position": v(132.29, 210.05) * mm});
            skLineSegment(sketch, "E3.2.4.16", {"start": v(126.6, 180.04) * mm, "end": v(103.51, 179.96) * mm});
            skCircle(sketch, "E3.2.4.19", {"center": v(115, 200) * mm, "radius": 25 * mm, "construction": true});
            skLineSegment(sketch, "E3.2.4.20", {"start": v(100.57, 225) * mm, "end": v(129.43, 225) * mm});
            skLineSegment(sketch, "E3.2.4.23", {"start": v(103.4, 219.96) * mm, "end": v(126.49, 220.04) * mm});
            skLineSegment(sketch, "E3.2.4.28", {"start": v(86.13, 200) * mm, "end": v(100.57, 225) * mm});
            skLineSegment(sketch, "E3.2.4.31", {"start": v(129.43, 225) * mm, "end": v(143.87, 200) * mm});
            skCircle(sketch, "E3.2.4.36", {"center": v(115, 200) * mm, "radius": 20 * mm, "construction": true});
            skLineSegment(sketch, "E3.2.4.38", {"start": v(91.9, 199.93) * mm, "end": v(103.4, 219.96) * mm});
            skLineSegment(sketch, "E3.2.4.39", {"start": v(103.51, 179.96) * mm, "end": v(91.9, 199.93) * mm});
            skLineSegment(sketch, "E3.2.4.40", {"start": v(138.1, 200.07) * mm, "end": v(126.6, 180.04) * mm});
            skLineSegment(sketch, "E3.2.4.41", {"start": v(126.49, 220.04) * mm, "end": v(138.1, 200.07) * mm});
            skLineSegment(sketch, "E3.2.5.7", {"start": v(100.57, 225) * mm, "end": v(86.13, 250) * mm});
            skLineSegment(sketch, "E3.2.5.9", {"start": v(129.43, 225) * mm, "end": v(100.57, 225) * mm});
            skLineSegment(sketch, "E3.2.5.10", {"start": v(143.87, 250) * mm, "end": v(129.43, 225) * mm});
            skPoint(sketch, "E3.2.5.12", {"position": v(115, 275) * mm});
            skPoint(sketch, "E3.2.5.13", {"position": v(132.29, 260.05) * mm});
            skLineSegment(sketch, "E3.2.5.16", {"start": v(126.6, 230.04) * mm, "end": v(103.51, 229.96) * mm});
            skCircle(sketch, "E3.2.5.19", {"center": v(115, 250) * mm, "radius": 25 * mm, "construction": true});
            skLineSegment(sketch, "E3.2.5.20", {"start": v(100.57, 275) * mm, "end": v(129.43, 275) * mm});
            skLineSegment(sketch, "E3.2.5.23", {"start": v(103.4, 269.96) * mm, "end": v(126.49, 270.04) * mm});
            skLineSegment(sketch, "E3.2.5.28", {"start": v(86.13, 250) * mm, "end": v(100.57, 275) * mm});
            skLineSegment(sketch, "E3.2.5.31", {"start": v(129.43, 275) * mm, "end": v(143.87, 250) * mm});
            skCircle(sketch, "E3.2.5.36", {"center": v(115, 250) * mm, "radius": 20 * mm, "construction": true});
            skLineSegment(sketch, "E3.2.5.38", {"start": v(91.9, 249.93) * mm, "end": v(103.4, 269.96) * mm});
            skLineSegment(sketch, "E3.2.5.39", {"start": v(103.51, 229.96) * mm, "end": v(91.9, 249.93) * mm});
            skLineSegment(sketch, "E3.2.5.40", {"start": v(138.1, 250.07) * mm, "end": v(126.6, 230.04) * mm});
            skLineSegment(sketch, "E3.2.5.41", {"start": v(126.49, 270.04) * mm, "end": v(138.1, 250.07) * mm});
            skLineSegment(sketch, "E3.2.6.7", {"start": v(100.57, 275) * mm, "end": v(86.13, 300) * mm});
            skLineSegment(sketch, "E3.2.6.9", {"start": v(129.43, 275) * mm, "end": v(100.57, 275) * mm});
            skLineSegment(sketch, "E3.2.6.10", {"start": v(143.87, 300) * mm, "end": v(129.43, 275) * mm});
            skPoint(sketch, "E3.2.6.12", {"position": v(115, 325) * mm});
            skPoint(sketch, "E3.2.6.13", {"position": v(132.29, 310.05) * mm});
            skLineSegment(sketch, "E3.2.6.16", {"start": v(126.6, 280.04) * mm, "end": v(103.51, 279.96) * mm});
            skCircle(sketch, "E3.2.6.19", {"center": v(115, 300) * mm, "radius": 25 * mm, "construction": true});
            skLineSegment(sketch, "E3.2.6.20", {"start": v(100.57, 325) * mm, "end": v(129.43, 325) * mm});
            skLineSegment(sketch, "E3.2.6.23", {"start": v(103.4, 319.96) * mm, "end": v(126.49, 320.04) * mm});
            skLineSegment(sketch, "E3.2.6.28", {"start": v(86.13, 300) * mm, "end": v(100.57, 325) * mm});
            skLineSegment(sketch, "E3.2.6.31", {"start": v(129.43, 325) * mm, "end": v(143.87, 300) * mm});
            skCircle(sketch, "E3.2.6.36", {"center": v(115, 300) * mm, "radius": 20 * mm, "construction": true});
            skLineSegment(sketch, "E3.2.6.38", {"start": v(91.9, 299.93) * mm, "end": v(103.4, 319.96) * mm});
            skLineSegment(sketch, "E3.2.6.39", {"start": v(103.51, 279.96) * mm, "end": v(91.9, 299.93) * mm});
            skLineSegment(sketch, "E3.2.6.40", {"start": v(138.1, 300.07) * mm, "end": v(126.6, 280.04) * mm});
            skLineSegment(sketch, "E3.2.6.41", {"start": v(126.49, 320.04) * mm, "end": v(138.1, 300.07) * mm});
            skLineSegment(sketch, "E3.2.7.7", {"start": v(100.57, 325) * mm, "end": v(86.13, 350) * mm});
            skLineSegment(sketch, "E3.2.7.9", {"start": v(129.43, 325) * mm, "end": v(100.57, 325) * mm});
            skLineSegment(sketch, "E3.2.7.10", {"start": v(143.87, 350) * mm, "end": v(129.43, 325) * mm});
            skPoint(sketch, "E3.2.7.12", {"position": v(115, 375) * mm});
            skPoint(sketch, "E3.2.7.13", {"position": v(132.29, 360.05) * mm});
            skLineSegment(sketch, "E3.2.7.16", {"start": v(126.6, 330.04) * mm, "end": v(103.51, 329.96) * mm});
            skCircle(sketch, "E3.2.7.19", {"center": v(115, 350) * mm, "radius": 25 * mm, "construction": true});
            skLineSegment(sketch, "E3.2.7.20", {"start": v(100.57, 375) * mm, "end": v(129.43, 375) * mm});
            skLineSegment(sketch, "E3.2.7.23", {"start": v(103.4, 369.96) * mm, "end": v(126.49, 370.04) * mm});
            skLineSegment(sketch, "E3.2.7.28", {"start": v(86.13, 350) * mm, "end": v(100.57, 375) * mm});
            skLineSegment(sketch, "E3.2.7.31", {"start": v(129.43, 375) * mm, "end": v(143.87, 350) * mm});
            skCircle(sketch, "E3.2.7.36", {"center": v(115, 350) * mm, "radius": 20 * mm, "construction": true});
            skLineSegment(sketch, "E3.2.7.38", {"start": v(91.9, 349.93) * mm, "end": v(103.4, 369.96) * mm});
            skLineSegment(sketch, "E3.2.7.39", {"start": v(103.51, 329.96) * mm, "end": v(91.9, 349.93) * mm});
            skLineSegment(sketch, "E3.2.7.40", {"start": v(138.1, 350.07) * mm, "end": v(126.6, 330.04) * mm});
            skLineSegment(sketch, "E3.2.7.41", {"start": v(126.49, 370.04) * mm, "end": v(138.1, 350.07) * mm});
            skLineSegment(sketch, "E3.2.8.7", {"start": v(100.57, 375) * mm, "end": v(86.13, 400) * mm});
            skLineSegment(sketch, "E3.2.8.9", {"start": v(129.43, 375) * mm, "end": v(100.57, 375) * mm});
            skLineSegment(sketch, "E3.2.8.10", {"start": v(143.87, 400) * mm, "end": v(129.43, 375) * mm});
            skPoint(sketch, "E3.2.8.12", {"position": v(115, 425) * mm});
            skPoint(sketch, "E3.2.8.13", {"position": v(132.29, 410.05) * mm});
            skLineSegment(sketch, "E3.2.8.16", {"start": v(126.6, 380.04) * mm, "end": v(103.51, 379.96) * mm});
            skCircle(sketch, "E3.2.8.19", {"center": v(115, 400) * mm, "radius": 25 * mm, "construction": true});
            skLineSegment(sketch, "E3.2.8.20", {"start": v(100.57, 425) * mm, "end": v(129.43, 425) * mm});
            skLineSegment(sketch, "E3.2.8.23", {"start": v(103.4, 419.96) * mm, "end": v(126.49, 420.04) * mm});
            skLineSegment(sketch, "E3.2.8.28", {"start": v(86.13, 400) * mm, "end": v(100.57, 425) * mm});
            skLineSegment(sketch, "E3.2.8.31", {"start": v(129.43, 425) * mm, "end": v(143.87, 400) * mm});
            skCircle(sketch, "E3.2.8.36", {"center": v(115, 400) * mm, "radius": 20 * mm, "construction": true});
            skLineSegment(sketch, "E3.2.8.38", {"start": v(91.9, 399.93) * mm, "end": v(103.4, 419.96) * mm});
            skLineSegment(sketch, "E3.2.8.39", {"start": v(103.51, 379.96) * mm, "end": v(91.9, 399.93) * mm});
            skLineSegment(sketch, "E3.2.8.40", {"start": v(138.1, 400.07) * mm, "end": v(126.6, 380.04) * mm});
            skLineSegment(sketch, "E3.2.8.41", {"start": v(126.49, 420.04) * mm, "end": v(138.1, 400.07) * mm});
            skLineSegment(sketch, "E3.2.9.7", {"start": v(100.57, 425) * mm, "end": v(86.13, 450) * mm});
            skLineSegment(sketch, "E3.2.9.9", {"start": v(129.43, 425) * mm, "end": v(100.57, 425) * mm});
            skLineSegment(sketch, "E3.2.9.10", {"start": v(143.87, 450) * mm, "end": v(129.43, 425) * mm});
            skPoint(sketch, "E3.2.9.12", {"position": v(115, 475) * mm});
            skPoint(sketch, "E3.2.9.13", {"position": v(132.29, 460.05) * mm});
            skLineSegment(sketch, "E3.2.9.16", {"start": v(126.6, 430.04) * mm, "end": v(103.51, 429.96) * mm});
            skCircle(sketch, "E3.2.9.19", {"center": v(115, 450) * mm, "radius": 25 * mm, "construction": true});
            skLineSegment(sketch, "E3.2.9.20", {"start": v(100.57, 475) * mm, "end": v(129.43, 475) * mm});
            skLineSegment(sketch, "E3.2.9.23", {"start": v(103.4, 469.96) * mm, "end": v(126.49, 470.04) * mm});
            skLineSegment(sketch, "E3.2.9.28", {"start": v(86.13, 450) * mm, "end": v(100.57, 475) * mm});
            skLineSegment(sketch, "E3.2.9.31", {"start": v(129.43, 475) * mm, "end": v(143.87, 450) * mm});
            skCircle(sketch, "E3.2.9.36", {"center": v(115, 450) * mm, "radius": 20 * mm, "construction": true});
            skLineSegment(sketch, "E3.2.9.38", {"start": v(91.9, 449.93) * mm, "end": v(103.4, 469.96) * mm});
            skLineSegment(sketch, "E3.2.9.39", {"start": v(103.51, 429.96) * mm, "end": v(91.9, 449.93) * mm});
            skLineSegment(sketch, "E3.2.9.40", {"start": v(138.1, 450.07) * mm, "end": v(126.6, 430.04) * mm});
            skLineSegment(sketch, "E3.2.9.41", {"start": v(126.49, 470.04) * mm, "end": v(138.1, 450.07) * mm});
            skLineSegment(sketch, "E3.3.0.7", {"start": v(158.07, -25) * mm, "end": v(143.63, 0) * mm});
            skLineSegment(sketch, "E3.3.0.9", {"start": v(186.93, -25) * mm, "end": v(158.07, -25) * mm});
            skLineSegment(sketch, "E3.3.0.10", {"start": v(201.37, 0) * mm, "end": v(186.93, -25) * mm});
            skPoint(sketch, "E3.3.0.12", {"position": v(172.5, 25) * mm});
            skPoint(sketch, "E3.3.0.13", {"position": v(189.79, 10.05) * mm});
            skLineSegment(sketch, "E3.3.0.16", {"start": v(184.1, -19.96) * mm, "end": v(161.01, -20.04) * mm});
            skCircle(sketch, "E3.3.0.19", {"center": v(172.5, 0) * mm, "radius": 25 * mm, "construction": true});
            skLineSegment(sketch, "E3.3.0.20", {"start": v(158.07, 25) * mm, "end": v(186.93, 25) * mm});
            skLineSegment(sketch, "E3.3.0.23", {"start": v(160.9, 19.96) * mm, "end": v(183.99, 20.04) * mm});
            skLineSegment(sketch, "E3.3.0.28", {"start": v(143.63, 0) * mm, "end": v(158.07, 25) * mm});
            skLineSegment(sketch, "E3.3.0.31", {"start": v(186.93, 25) * mm, "end": v(201.37, 0) * mm});
            skCircle(sketch, "E3.3.0.36", {"center": v(172.5, 0) * mm, "radius": 20 * mm, "construction": true});
            skLineSegment(sketch, "E3.3.0.38", {"start": v(149.4, -0.07) * mm, "end": v(160.9, 19.96) * mm});
            skLineSegment(sketch, "E3.3.0.39", {"start": v(161.01, -20.04) * mm, "end": v(149.4, -0.07) * mm});
            skLineSegment(sketch, "E3.3.0.40", {"start": v(195.6, 0.07) * mm, "end": v(184.1, -19.96) * mm});
            skLineSegment(sketch, "E3.3.0.41", {"start": v(183.99, 20.04) * mm, "end": v(195.6, 0.07) * mm});
            skLineSegment(sketch, "E3.3.1.7", {"start": v(158.07, 25) * mm, "end": v(143.63, 50) * mm});
            skLineSegment(sketch, "E3.3.1.9", {"start": v(186.93, 25) * mm, "end": v(158.07, 25) * mm});
            skLineSegment(sketch, "E3.3.1.10", {"start": v(201.37, 50) * mm, "end": v(186.93, 25) * mm});
            skPoint(sketch, "E3.3.1.12", {"position": v(172.5, 75) * mm});
            skPoint(sketch, "E3.3.1.13", {"position": v(189.79, 60.05) * mm});
            skLineSegment(sketch, "E3.3.1.16", {"start": v(184.1, 30.04) * mm, "end": v(161.01, 29.96) * mm});
            skCircle(sketch, "E3.3.1.19", {"center": v(172.5, 50) * mm, "radius": 25 * mm, "construction": true});
            skLineSegment(sketch, "E3.3.1.20", {"start": v(158.07, 75) * mm, "end": v(186.93, 75) * mm});
            skLineSegment(sketch, "E3.3.1.23", {"start": v(160.9, 69.96) * mm, "end": v(183.99, 70.04) * mm});
            skLineSegment(sketch, "E3.3.1.28", {"start": v(143.63, 50) * mm, "end": v(158.07, 75) * mm});
            skLineSegment(sketch, "E3.3.1.31", {"start": v(186.93, 75) * mm, "end": v(201.37, 50) * mm});
            skCircle(sketch, "E3.3.1.36", {"center": v(172.5, 50) * mm, "radius": 20 * mm, "construction": true});
            skLineSegment(sketch, "E3.3.1.38", {"start": v(149.4, 49.93) * mm, "end": v(160.9, 69.96) * mm});
            skLineSegment(sketch, "E3.3.1.39", {"start": v(161.01, 29.96) * mm, "end": v(149.4, 49.93) * mm});
            skLineSegment(sketch, "E3.3.1.40", {"start": v(195.6, 50.07) * mm, "end": v(184.1, 30.04) * mm});
            skLineSegment(sketch, "E3.3.1.41", {"start": v(183.99, 70.04) * mm, "end": v(195.6, 50.07) * mm});
            skLineSegment(sketch, "E3.3.2.7", {"start": v(158.07, 75) * mm, "end": v(143.63, 100) * mm});
            skLineSegment(sketch, "E3.3.2.9", {"start": v(186.93, 75) * mm, "end": v(158.07, 75) * mm});
            skLineSegment(sketch, "E3.3.2.10", {"start": v(201.37, 100) * mm, "end": v(186.93, 75) * mm});
            skPoint(sketch, "E3.3.2.12", {"position": v(172.5, 125) * mm});
            skPoint(sketch, "E3.3.2.13", {"position": v(189.79, 110.05) * mm});
            skLineSegment(sketch, "E3.3.2.16", {"start": v(184.1, 80.04) * mm, "end": v(161.01, 79.96) * mm});
            skCircle(sketch, "E3.3.2.19", {"center": v(172.5, 100) * mm, "radius": 25 * mm, "construction": true});
            skLineSegment(sketch, "E3.3.2.20", {"start": v(158.07, 125) * mm, "end": v(186.93, 125) * mm});
            skLineSegment(sketch, "E3.3.2.23", {"start": v(160.9, 119.96) * mm, "end": v(183.99, 120.04) * mm});
            skLineSegment(sketch, "E3.3.2.28", {"start": v(143.63, 100) * mm, "end": v(158.07, 125) * mm});
            skLineSegment(sketch, "E3.3.2.31", {"start": v(186.93, 125) * mm, "end": v(201.37, 100) * mm});
            skCircle(sketch, "E3.3.2.36", {"center": v(172.5, 100) * mm, "radius": 20 * mm, "construction": true});
            skLineSegment(sketch, "E3.3.2.38", {"start": v(149.4, 99.93) * mm, "end": v(160.9, 119.96) * mm});
            skLineSegment(sketch, "E3.3.2.39", {"start": v(161.01, 79.96) * mm, "end": v(149.4, 99.93) * mm});
            skLineSegment(sketch, "E3.3.2.40", {"start": v(195.6, 100.07) * mm, "end": v(184.1, 80.04) * mm});
            skLineSegment(sketch, "E3.3.2.41", {"start": v(183.99, 120.04) * mm, "end": v(195.6, 100.07) * mm});
            skLineSegment(sketch, "E3.3.3.7", {"start": v(158.07, 125) * mm, "end": v(143.63, 150) * mm});
            skLineSegment(sketch, "E3.3.3.9", {"start": v(186.93, 125) * mm, "end": v(158.07, 125) * mm});
            skLineSegment(sketch, "E3.3.3.10", {"start": v(201.37, 150) * mm, "end": v(186.93, 125) * mm});
            skPoint(sketch, "E3.3.3.12", {"position": v(172.5, 175) * mm});
            skPoint(sketch, "E3.3.3.13", {"position": v(189.79, 160.05) * mm});
            skLineSegment(sketch, "E3.3.3.16", {"start": v(184.1, 130.04) * mm, "end": v(161.01, 129.96) * mm});
            skCircle(sketch, "E3.3.3.19", {"center": v(172.5, 150) * mm, "radius": 25 * mm, "construction": true});
            skLineSegment(sketch, "E3.3.3.20", {"start": v(158.07, 175) * mm, "end": v(186.93, 175) * mm});
            skLineSegment(sketch, "E3.3.3.23", {"start": v(160.9, 169.96) * mm, "end": v(183.99, 170.04) * mm});
            skLineSegment(sketch, "E3.3.3.28", {"start": v(143.63, 150) * mm, "end": v(158.07, 175) * mm});
            skLineSegment(sketch, "E3.3.3.31", {"start": v(186.93, 175) * mm, "end": v(201.37, 150) * mm});
            skCircle(sketch, "E3.3.3.36", {"center": v(172.5, 150) * mm, "radius": 20 * mm, "construction": true});
            skLineSegment(sketch, "E3.3.3.38", {"start": v(149.4, 149.93) * mm, "end": v(160.9, 169.96) * mm});
            skLineSegment(sketch, "E3.3.3.39", {"start": v(161.01, 129.96) * mm, "end": v(149.4, 149.93) * mm});
            skLineSegment(sketch, "E3.3.3.40", {"start": v(195.6, 150.07) * mm, "end": v(184.1, 130.04) * mm});
            skLineSegment(sketch, "E3.3.3.41", {"start": v(183.99, 170.04) * mm, "end": v(195.6, 150.07) * mm});
            skLineSegment(sketch, "E3.3.4.7", {"start": v(158.07, 175) * mm, "end": v(143.63, 200) * mm});
            skLineSegment(sketch, "E3.3.4.9", {"start": v(186.93, 175) * mm, "end": v(158.07, 175) * mm});
            skLineSegment(sketch, "E3.3.4.10", {"start": v(201.37, 200) * mm, "end": v(186.93, 175) * mm});
            skPoint(sketch, "E3.3.4.12", {"position": v(172.5, 225) * mm});
            skPoint(sketch, "E3.3.4.13", {"position": v(189.79, 210.05) * mm});
            skLineSegment(sketch, "E3.3.4.16", {"start": v(184.1, 180.04) * mm, "end": v(161.01, 179.96) * mm});
            skCircle(sketch, "E3.3.4.19", {"center": v(172.5, 200) * mm, "radius": 25 * mm, "construction": true});
            skLineSegment(sketch, "E3.3.4.20", {"start": v(158.07, 225) * mm, "end": v(186.93, 225) * mm});
            skLineSegment(sketch, "E3.3.4.23", {"start": v(160.9, 219.96) * mm, "end": v(183.99, 220.04) * mm});
            skLineSegment(sketch, "E3.3.4.28", {"start": v(143.63, 200) * mm, "end": v(158.07, 225) * mm});
            skLineSegment(sketch, "E3.3.4.31", {"start": v(186.93, 225) * mm, "end": v(201.37, 200) * mm});
            skCircle(sketch, "E3.3.4.36", {"center": v(172.5, 200) * mm, "radius": 20 * mm, "construction": true});
            skLineSegment(sketch, "E3.3.4.38", {"start": v(149.4, 199.93) * mm, "end": v(160.9, 219.96) * mm});
            skLineSegment(sketch, "E3.3.4.39", {"start": v(161.01, 179.96) * mm, "end": v(149.4, 199.93) * mm});
            skLineSegment(sketch, "E3.3.4.40", {"start": v(195.6, 200.07) * mm, "end": v(184.1, 180.04) * mm});
            skLineSegment(sketch, "E3.3.4.41", {"start": v(183.99, 220.04) * mm, "end": v(195.6, 200.07) * mm});
            skLineSegment(sketch, "E3.3.5.7", {"start": v(158.07, 225) * mm, "end": v(143.63, 250) * mm});
            skLineSegment(sketch, "E3.3.5.9", {"start": v(186.93, 225) * mm, "end": v(158.07, 225) * mm});
            skLineSegment(sketch, "E3.3.5.10", {"start": v(201.37, 250) * mm, "end": v(186.93, 225) * mm});
            skPoint(sketch, "E3.3.5.12", {"position": v(172.5, 275) * mm});
            skPoint(sketch, "E3.3.5.13", {"position": v(189.79, 260.05) * mm});
            skLineSegment(sketch, "E3.3.5.16", {"start": v(184.1, 230.04) * mm, "end": v(161.01, 229.96) * mm});
            skCircle(sketch, "E3.3.5.19", {"center": v(172.5, 250) * mm, "radius": 25 * mm, "construction": true});
            skLineSegment(sketch, "E3.3.5.20", {"start": v(158.07, 275) * mm, "end": v(186.93, 275) * mm});
            skLineSegment(sketch, "E3.3.5.23", {"start": v(160.9, 269.96) * mm, "end": v(183.99, 270.04) * mm});
            skLineSegment(sketch, "E3.3.5.28", {"start": v(143.63, 250) * mm, "end": v(158.07, 275) * mm});
            skLineSegment(sketch, "E3.3.5.31", {"start": v(186.93, 275) * mm, "end": v(201.37, 250) * mm});
            skCircle(sketch, "E3.3.5.36", {"center": v(172.5, 250) * mm, "radius": 20 * mm, "construction": true});
            skLineSegment(sketch, "E3.3.5.38", {"start": v(149.4, 249.93) * mm, "end": v(160.9, 269.96) * mm});
            skLineSegment(sketch, "E3.3.5.39", {"start": v(161.01, 229.96) * mm, "end": v(149.4, 249.93) * mm});
            skLineSegment(sketch, "E3.3.5.40", {"start": v(195.6, 250.07) * mm, "end": v(184.1, 230.04) * mm});
            skLineSegment(sketch, "E3.3.5.41", {"start": v(183.99, 270.04) * mm, "end": v(195.6, 250.07) * mm});
            skLineSegment(sketch, "E3.3.6.7", {"start": v(158.07, 275) * mm, "end": v(143.63, 300) * mm});
            skLineSegment(sketch, "E3.3.6.9", {"start": v(186.93, 275) * mm, "end": v(158.07, 275) * mm});
            skLineSegment(sketch, "E3.3.6.10", {"start": v(201.37, 300) * mm, "end": v(186.93, 275) * mm});
            skPoint(sketch, "E3.3.6.12", {"position": v(172.5, 325) * mm});
            skPoint(sketch, "E3.3.6.13", {"position": v(189.79, 310.05) * mm});
            skLineSegment(sketch, "E3.3.6.16", {"start": v(184.1, 280.04) * mm, "end": v(161.01, 279.96) * mm});
            skCircle(sketch, "E3.3.6.19", {"center": v(172.5, 300) * mm, "radius": 25 * mm, "construction": true});
            skLineSegment(sketch, "E3.3.6.20", {"start": v(158.07, 325) * mm, "end": v(186.93, 325) * mm});
            skLineSegment(sketch, "E3.3.6.23", {"start": v(160.9, 319.96) * mm, "end": v(183.99, 320.04) * mm});
            skLineSegment(sketch, "E3.3.6.28", {"start": v(143.63, 300) * mm, "end": v(158.07, 325) * mm});
            skLineSegment(sketch, "E3.3.6.31", {"start": v(186.93, 325) * mm, "end": v(201.37, 300) * mm});
            skCircle(sketch, "E3.3.6.36", {"center": v(172.5, 300) * mm, "radius": 20 * mm, "construction": true});
            skLineSegment(sketch, "E3.3.6.38", {"start": v(149.4, 299.93) * mm, "end": v(160.9, 319.96) * mm});
            skLineSegment(sketch, "E3.3.6.39", {"start": v(161.01, 279.96) * mm, "end": v(149.4, 299.93) * mm});
            skLineSegment(sketch, "E3.3.6.40", {"start": v(195.6, 300.07) * mm, "end": v(184.1, 280.04) * mm});
            skLineSegment(sketch, "E3.3.6.41", {"start": v(183.99, 320.04) * mm, "end": v(195.6, 300.07) * mm});
            skLineSegment(sketch, "E3.3.7.7", {"start": v(158.07, 325) * mm, "end": v(143.63, 350) * mm});
            skLineSegment(sketch, "E3.3.7.9", {"start": v(186.93, 325) * mm, "end": v(158.07, 325) * mm});
            skLineSegment(sketch, "E3.3.7.10", {"start": v(201.37, 350) * mm, "end": v(186.93, 325) * mm});
            skPoint(sketch, "E3.3.7.12", {"position": v(172.5, 375) * mm});
            skPoint(sketch, "E3.3.7.13", {"position": v(189.79, 360.05) * mm});
            skLineSegment(sketch, "E3.3.7.16", {"start": v(184.1, 330.04) * mm, "end": v(161.01, 329.96) * mm});
            skCircle(sketch, "E3.3.7.19", {"center": v(172.5, 350) * mm, "radius": 25 * mm, "construction": true});
            skLineSegment(sketch, "E3.3.7.20", {"start": v(158.07, 375) * mm, "end": v(186.93, 375) * mm});
            skLineSegment(sketch, "E3.3.7.23", {"start": v(160.9, 369.96) * mm, "end": v(183.99, 370.04) * mm});
            skLineSegment(sketch, "E3.3.7.28", {"start": v(143.63, 350) * mm, "end": v(158.07, 375) * mm});
            skLineSegment(sketch, "E3.3.7.31", {"start": v(186.93, 375) * mm, "end": v(201.37, 350) * mm});
            skCircle(sketch, "E3.3.7.36", {"center": v(172.5, 350) * mm, "radius": 20 * mm, "construction": true});
            skLineSegment(sketch, "E3.3.7.38", {"start": v(149.4, 349.93) * mm, "end": v(160.9, 369.96) * mm});
            skLineSegment(sketch, "E3.3.7.39", {"start": v(161.01, 329.96) * mm, "end": v(149.4, 349.93) * mm});
            skLineSegment(sketch, "E3.3.7.40", {"start": v(195.6, 350.07) * mm, "end": v(184.1, 330.04) * mm});
            skLineSegment(sketch, "E3.3.7.41", {"start": v(183.99, 370.04) * mm, "end": v(195.6, 350.07) * mm});
            skLineSegment(sketch, "E3.3.8.7", {"start": v(158.07, 375) * mm, "end": v(143.63, 400) * mm});
            skLineSegment(sketch, "E3.3.8.9", {"start": v(186.93, 375) * mm, "end": v(158.07, 375) * mm});
            skLineSegment(sketch, "E3.3.8.10", {"start": v(201.37, 400) * mm, "end": v(186.93, 375) * mm});
            skPoint(sketch, "E3.3.8.12", {"position": v(172.5, 425) * mm});
            skPoint(sketch, "E3.3.8.13", {"position": v(189.79, 410.05) * mm});
            skLineSegment(sketch, "E3.3.8.16", {"start": v(184.1, 380.04) * mm, "end": v(161.01, 379.96) * mm});
            skCircle(sketch, "E3.3.8.19", {"center": v(172.5, 400) * mm, "radius": 25 * mm, "construction": true});
            skLineSegment(sketch, "E3.3.8.20", {"start": v(158.07, 425) * mm, "end": v(186.93, 425) * mm});
            skLineSegment(sketch, "E3.3.8.23", {"start": v(160.9, 419.96) * mm, "end": v(183.99, 420.04) * mm});
            skLineSegment(sketch, "E3.3.8.28", {"start": v(143.63, 400) * mm, "end": v(158.07, 425) * mm});
            skLineSegment(sketch, "E3.3.8.31", {"start": v(186.93, 425) * mm, "end": v(201.37, 400) * mm});
            skCircle(sketch, "E3.3.8.36", {"center": v(172.5, 400) * mm, "radius": 20 * mm, "construction": true});
            skLineSegment(sketch, "E3.3.8.38", {"start": v(149.4, 399.93) * mm, "end": v(160.9, 419.96) * mm});
            skLineSegment(sketch, "E3.3.8.39", {"start": v(161.01, 379.96) * mm, "end": v(149.4, 399.93) * mm});
            skLineSegment(sketch, "E3.3.8.40", {"start": v(195.6, 400.07) * mm, "end": v(184.1, 380.04) * mm});
            skLineSegment(sketch, "E3.3.8.41", {"start": v(183.99, 420.04) * mm, "end": v(195.6, 400.07) * mm});
            skLineSegment(sketch, "E3.3.9.7", {"start": v(158.07, 425) * mm, "end": v(143.63, 450) * mm});
            skLineSegment(sketch, "E3.3.9.9", {"start": v(186.93, 425) * mm, "end": v(158.07, 425) * mm});
            skLineSegment(sketch, "E3.3.9.10", {"start": v(201.37, 450) * mm, "end": v(186.93, 425) * mm});
            skPoint(sketch, "E3.3.9.12", {"position": v(172.5, 475) * mm});
            skPoint(sketch, "E3.3.9.13", {"position": v(189.79, 460.05) * mm});
            skLineSegment(sketch, "E3.3.9.16", {"start": v(184.1, 430.04) * mm, "end": v(161.01, 429.96) * mm});
            skCircle(sketch, "E3.3.9.19", {"center": v(172.5, 450) * mm, "radius": 25 * mm, "construction": true});
            skLineSegment(sketch, "E3.3.9.20", {"start": v(158.07, 475) * mm, "end": v(186.93, 475) * mm});
            skLineSegment(sketch, "E3.3.9.23", {"start": v(160.9, 469.96) * mm, "end": v(183.99, 470.04) * mm});
            skLineSegment(sketch, "E3.3.9.28", {"start": v(143.63, 450) * mm, "end": v(158.07, 475) * mm});
            skLineSegment(sketch, "E3.3.9.31", {"start": v(186.93, 475) * mm, "end": v(201.37, 450) * mm});
            skCircle(sketch, "E3.3.9.36", {"center": v(172.5, 450) * mm, "radius": 20 * mm, "construction": true});
            skLineSegment(sketch, "E3.3.9.38", {"start": v(149.4, 449.93) * mm, "end": v(160.9, 469.96) * mm});
            skLineSegment(sketch, "E3.3.9.39", {"start": v(161.01, 429.96) * mm, "end": v(149.4, 449.93) * mm});
            skLineSegment(sketch, "E3.3.9.40", {"start": v(195.6, 450.07) * mm, "end": v(184.1, 430.04) * mm});
            skLineSegment(sketch, "E3.3.9.41", {"start": v(183.99, 470.04) * mm, "end": v(195.6, 450.07) * mm});
            skLineSegment(sketch, "E3.4.0.7", {"start": v(215.57, -25) * mm, "end": v(201.13, 0) * mm});
            skLineSegment(sketch, "E3.4.0.9", {"start": v(244.43, -25) * mm, "end": v(215.57, -25) * mm});
            skLineSegment(sketch, "E3.4.0.10", {"start": v(258.87, 0) * mm, "end": v(244.43, -25) * mm});
            skPoint(sketch, "E3.4.0.12", {"position": v(230, 25) * mm});
            skPoint(sketch, "E3.4.0.13", {"position": v(247.29, 10.05) * mm});
            skLineSegment(sketch, "E3.4.0.16", {"start": v(241.6, -19.96) * mm, "end": v(218.51, -20.04) * mm});
            skCircle(sketch, "E3.4.0.19", {"center": v(230, 0) * mm, "radius": 25 * mm, "construction": true});
            skLineSegment(sketch, "E3.4.0.20", {"start": v(215.57, 25) * mm, "end": v(244.43, 25) * mm});
            skLineSegment(sketch, "E3.4.0.23", {"start": v(218.4, 19.96) * mm, "end": v(241.49, 20.04) * mm});
            skLineSegment(sketch, "E3.4.0.28", {"start": v(201.13, 0) * mm, "end": v(215.57, 25) * mm});
            skLineSegment(sketch, "E3.4.0.31", {"start": v(244.43, 25) * mm, "end": v(258.87, 0) * mm});
            skCircle(sketch, "E3.4.0.36", {"center": v(230, 0) * mm, "radius": 20 * mm, "construction": true});
            skLineSegment(sketch, "E3.4.0.38", {"start": v(206.9, -0.07) * mm, "end": v(218.4, 19.96) * mm});
            skLineSegment(sketch, "E3.4.0.39", {"start": v(218.51, -20.04) * mm, "end": v(206.9, -0.07) * mm});
            skLineSegment(sketch, "E3.4.0.40", {"start": v(253.1, 0.07) * mm, "end": v(241.6, -19.96) * mm});
            skLineSegment(sketch, "E3.4.0.41", {"start": v(241.49, 20.04) * mm, "end": v(253.1, 0.07) * mm});
            skLineSegment(sketch, "E3.4.1.7", {"start": v(215.57, 25) * mm, "end": v(201.13, 50) * mm});
            skLineSegment(sketch, "E3.4.1.9", {"start": v(244.43, 25) * mm, "end": v(215.57, 25) * mm});
            skLineSegment(sketch, "E3.4.1.10", {"start": v(258.87, 50) * mm, "end": v(244.43, 25) * mm});
            skPoint(sketch, "E3.4.1.12", {"position": v(230, 75) * mm});
            skPoint(sketch, "E3.4.1.13", {"position": v(247.29, 60.05) * mm});
            skLineSegment(sketch, "E3.4.1.16", {"start": v(241.6, 30.04) * mm, "end": v(218.51, 29.96) * mm});
            skCircle(sketch, "E3.4.1.19", {"center": v(230, 50) * mm, "radius": 25 * mm, "construction": true});
            skLineSegment(sketch, "E3.4.1.20", {"start": v(215.57, 75) * mm, "end": v(244.43, 75) * mm});
            skLineSegment(sketch, "E3.4.1.23", {"start": v(218.4, 69.96) * mm, "end": v(241.49, 70.04) * mm});
            skLineSegment(sketch, "E3.4.1.28", {"start": v(201.13, 50) * mm, "end": v(215.57, 75) * mm});
            skLineSegment(sketch, "E3.4.1.31", {"start": v(244.43, 75) * mm, "end": v(258.87, 50) * mm});
            skCircle(sketch, "E3.4.1.36", {"center": v(230, 50) * mm, "radius": 20 * mm, "construction": true});
            skLineSegment(sketch, "E3.4.1.38", {"start": v(206.9, 49.93) * mm, "end": v(218.4, 69.96) * mm});
            skLineSegment(sketch, "E3.4.1.39", {"start": v(218.51, 29.96) * mm, "end": v(206.9, 49.93) * mm});
            skLineSegment(sketch, "E3.4.1.40", {"start": v(253.1, 50.07) * mm, "end": v(241.6, 30.04) * mm});
            skLineSegment(sketch, "E3.4.1.41", {"start": v(241.49, 70.04) * mm, "end": v(253.1, 50.07) * mm});
            skLineSegment(sketch, "E3.4.2.7", {"start": v(215.57, 75) * mm, "end": v(201.13, 100) * mm});
            skLineSegment(sketch, "E3.4.2.9", {"start": v(244.43, 75) * mm, "end": v(215.57, 75) * mm});
            skLineSegment(sketch, "E3.4.2.10", {"start": v(258.87, 100) * mm, "end": v(244.43, 75) * mm});
            skPoint(sketch, "E3.4.2.12", {"position": v(230, 125) * mm});
            skPoint(sketch, "E3.4.2.13", {"position": v(247.29, 110.05) * mm});
            skLineSegment(sketch, "E3.4.2.16", {"start": v(241.6, 80.04) * mm, "end": v(218.51, 79.96) * mm});
            skCircle(sketch, "E3.4.2.19", {"center": v(230, 100) * mm, "radius": 25 * mm, "construction": true});
            skLineSegment(sketch, "E3.4.2.20", {"start": v(215.57, 125) * mm, "end": v(244.43, 125) * mm});
            skLineSegment(sketch, "E3.4.2.23", {"start": v(218.4, 119.96) * mm, "end": v(241.49, 120.04) * mm});
            skLineSegment(sketch, "E3.4.2.28", {"start": v(201.13, 100) * mm, "end": v(215.57, 125) * mm});
            skLineSegment(sketch, "E3.4.2.31", {"start": v(244.43, 125) * mm, "end": v(258.87, 100) * mm});
            skCircle(sketch, "E3.4.2.36", {"center": v(230, 100) * mm, "radius": 20 * mm, "construction": true});
            skLineSegment(sketch, "E3.4.2.38", {"start": v(206.9, 99.93) * mm, "end": v(218.4, 119.96) * mm});
            skLineSegment(sketch, "E3.4.2.39", {"start": v(218.51, 79.96) * mm, "end": v(206.9, 99.93) * mm});
            skLineSegment(sketch, "E3.4.2.40", {"start": v(253.1, 100.07) * mm, "end": v(241.6, 80.04) * mm});
            skLineSegment(sketch, "E3.4.2.41", {"start": v(241.49, 120.04) * mm, "end": v(253.1, 100.07) * mm});
            skLineSegment(sketch, "E3.4.3.7", {"start": v(215.57, 125) * mm, "end": v(201.13, 150) * mm});
            skLineSegment(sketch, "E3.4.3.9", {"start": v(244.43, 125) * mm, "end": v(215.57, 125) * mm});
            skLineSegment(sketch, "E3.4.3.10", {"start": v(258.87, 150) * mm, "end": v(244.43, 125) * mm});
            skPoint(sketch, "E3.4.3.12", {"position": v(230, 175) * mm});
            skPoint(sketch, "E3.4.3.13", {"position": v(247.29, 160.05) * mm});
            skLineSegment(sketch, "E3.4.3.16", {"start": v(241.6, 130.04) * mm, "end": v(218.51, 129.96) * mm});
            skCircle(sketch, "E3.4.3.19", {"center": v(230, 150) * mm, "radius": 25 * mm, "construction": true});
            skLineSegment(sketch, "E3.4.3.20", {"start": v(215.57, 175) * mm, "end": v(244.43, 175) * mm});
            skLineSegment(sketch, "E3.4.3.23", {"start": v(218.4, 169.96) * mm, "end": v(241.49, 170.04) * mm});
            skLineSegment(sketch, "E3.4.3.28", {"start": v(201.13, 150) * mm, "end": v(215.57, 175) * mm});
            skLineSegment(sketch, "E3.4.3.31", {"start": v(244.43, 175) * mm, "end": v(258.87, 150) * mm});
            skCircle(sketch, "E3.4.3.36", {"center": v(230, 150) * mm, "radius": 20 * mm, "construction": true});
            skLineSegment(sketch, "E3.4.3.38", {"start": v(206.9, 149.93) * mm, "end": v(218.4, 169.96) * mm});
            skLineSegment(sketch, "E3.4.3.39", {"start": v(218.51, 129.96) * mm, "end": v(206.9, 149.93) * mm});
            skLineSegment(sketch, "E3.4.3.40", {"start": v(253.1, 150.07) * mm, "end": v(241.6, 130.04) * mm});
            skLineSegment(sketch, "E3.4.3.41", {"start": v(241.49, 170.04) * mm, "end": v(253.1, 150.07) * mm});
            skLineSegment(sketch, "E3.4.4.7", {"start": v(215.57, 175) * mm, "end": v(201.13, 200) * mm});
            skLineSegment(sketch, "E3.4.4.9", {"start": v(244.43, 175) * mm, "end": v(215.57, 175) * mm});
            skLineSegment(sketch, "E3.4.4.10", {"start": v(258.87, 200) * mm, "end": v(244.43, 175) * mm});
            skPoint(sketch, "E3.4.4.12", {"position": v(230, 225) * mm});
            skPoint(sketch, "E3.4.4.13", {"position": v(247.29, 210.05) * mm});
            skLineSegment(sketch, "E3.4.4.16", {"start": v(241.6, 180.04) * mm, "end": v(218.51, 179.96) * mm});
            skCircle(sketch, "E3.4.4.19", {"center": v(230, 200) * mm, "radius": 25 * mm, "construction": true});
            skLineSegment(sketch, "E3.4.4.20", {"start": v(215.57, 225) * mm, "end": v(244.43, 225) * mm});
            skLineSegment(sketch, "E3.4.4.23", {"start": v(218.4, 219.96) * mm, "end": v(241.49, 220.04) * mm});
            skLineSegment(sketch, "E3.4.4.28", {"start": v(201.13, 200) * mm, "end": v(215.57, 225) * mm});
            skLineSegment(sketch, "E3.4.4.31", {"start": v(244.43, 225) * mm, "end": v(258.87, 200) * mm});
            skCircle(sketch, "E3.4.4.36", {"center": v(230, 200) * mm, "radius": 20 * mm, "construction": true});
            skLineSegment(sketch, "E3.4.4.38", {"start": v(206.9, 199.93) * mm, "end": v(218.4, 219.96) * mm});
            skLineSegment(sketch, "E3.4.4.39", {"start": v(218.51, 179.96) * mm, "end": v(206.9, 199.93) * mm});
            skLineSegment(sketch, "E3.4.4.40", {"start": v(253.1, 200.07) * mm, "end": v(241.6, 180.04) * mm});
            skLineSegment(sketch, "E3.4.4.41", {"start": v(241.49, 220.04) * mm, "end": v(253.1, 200.07) * mm});
            skLineSegment(sketch, "E3.4.5.7", {"start": v(215.57, 225) * mm, "end": v(201.13, 250) * mm});
            skLineSegment(sketch, "E3.4.5.9", {"start": v(244.43, 225) * mm, "end": v(215.57, 225) * mm});
            skLineSegment(sketch, "E3.4.5.10", {"start": v(258.87, 250) * mm, "end": v(244.43, 225) * mm});
            skPoint(sketch, "E3.4.5.12", {"position": v(230, 275) * mm});
            skPoint(sketch, "E3.4.5.13", {"position": v(247.29, 260.05) * mm});
            skLineSegment(sketch, "E3.4.5.16", {"start": v(241.6, 230.04) * mm, "end": v(218.51, 229.96) * mm});
            skCircle(sketch, "E3.4.5.19", {"center": v(230, 250) * mm, "radius": 25 * mm, "construction": true});
            skLineSegment(sketch, "E3.4.5.20", {"start": v(215.57, 275) * mm, "end": v(244.43, 275) * mm});
            skLineSegment(sketch, "E3.4.5.23", {"start": v(218.4, 269.96) * mm, "end": v(241.49, 270.04) * mm});
            skLineSegment(sketch, "E3.4.5.28", {"start": v(201.13, 250) * mm, "end": v(215.57, 275) * mm});
            skLineSegment(sketch, "E3.4.5.31", {"start": v(244.43, 275) * mm, "end": v(258.87, 250) * mm});
            skCircle(sketch, "E3.4.5.36", {"center": v(230, 250) * mm, "radius": 20 * mm, "construction": true});
            skLineSegment(sketch, "E3.4.5.38", {"start": v(206.9, 249.93) * mm, "end": v(218.4, 269.96) * mm});
            skLineSegment(sketch, "E3.4.5.39", {"start": v(218.51, 229.96) * mm, "end": v(206.9, 249.93) * mm});
            skLineSegment(sketch, "E3.4.5.40", {"start": v(253.1, 250.07) * mm, "end": v(241.6, 230.04) * mm});
            skLineSegment(sketch, "E3.4.5.41", {"start": v(241.49, 270.04) * mm, "end": v(253.1, 250.07) * mm});
            skLineSegment(sketch, "E3.4.6.7", {"start": v(215.57, 275) * mm, "end": v(201.13, 300) * mm});
            skLineSegment(sketch, "E3.4.6.9", {"start": v(244.43, 275) * mm, "end": v(215.57, 275) * mm});
            skLineSegment(sketch, "E3.4.6.10", {"start": v(258.87, 300) * mm, "end": v(244.43, 275) * mm});
            skPoint(sketch, "E3.4.6.12", {"position": v(230, 325) * mm});
            skPoint(sketch, "E3.4.6.13", {"position": v(247.29, 310.05) * mm});
            skLineSegment(sketch, "E3.4.6.16", {"start": v(241.6, 280.04) * mm, "end": v(218.51, 279.96) * mm});
            skCircle(sketch, "E3.4.6.19", {"center": v(230, 300) * mm, "radius": 25 * mm, "construction": true});
            skLineSegment(sketch, "E3.4.6.20", {"start": v(215.57, 325) * mm, "end": v(244.43, 325) * mm});
            skLineSegment(sketch, "E3.4.6.23", {"start": v(218.4, 319.96) * mm, "end": v(241.49, 320.04) * mm});
            skLineSegment(sketch, "E3.4.6.28", {"start": v(201.13, 300) * mm, "end": v(215.57, 325) * mm});
            skLineSegment(sketch, "E3.4.6.31", {"start": v(244.43, 325) * mm, "end": v(258.87, 300) * mm});
            skCircle(sketch, "E3.4.6.36", {"center": v(230, 300) * mm, "radius": 20 * mm, "construction": true});
            skLineSegment(sketch, "E3.4.6.38", {"start": v(206.9, 299.93) * mm, "end": v(218.4, 319.96) * mm});
            skLineSegment(sketch, "E3.4.6.39", {"start": v(218.51, 279.96) * mm, "end": v(206.9, 299.93) * mm});
            skLineSegment(sketch, "E3.4.6.40", {"start": v(253.1, 300.07) * mm, "end": v(241.6, 280.04) * mm});
            skLineSegment(sketch, "E3.4.6.41", {"start": v(241.49, 320.04) * mm, "end": v(253.1, 300.07) * mm});
            skLineSegment(sketch, "E3.4.7.7", {"start": v(215.57, 325) * mm, "end": v(201.13, 350) * mm});
            skLineSegment(sketch, "E3.4.7.9", {"start": v(244.43, 325) * mm, "end": v(215.57, 325) * mm});
            skLineSegment(sketch, "E3.4.7.10", {"start": v(258.87, 350) * mm, "end": v(244.43, 325) * mm});
            skPoint(sketch, "E3.4.7.12", {"position": v(230, 375) * mm});
            skPoint(sketch, "E3.4.7.13", {"position": v(247.29, 360.05) * mm});
            skLineSegment(sketch, "E3.4.7.16", {"start": v(241.6, 330.04) * mm, "end": v(218.51, 329.96) * mm});
            skCircle(sketch, "E3.4.7.19", {"center": v(230, 350) * mm, "radius": 25 * mm, "construction": true});
            skLineSegment(sketch, "E3.4.7.20", {"start": v(215.57, 375) * mm, "end": v(244.43, 375) * mm});
            skLineSegment(sketch, "E3.4.7.23", {"start": v(218.4, 369.96) * mm, "end": v(241.49, 370.04) * mm});
            skLineSegment(sketch, "E3.4.7.28", {"start": v(201.13, 350) * mm, "end": v(215.57, 375) * mm});
            skLineSegment(sketch, "E3.4.7.31", {"start": v(244.43, 375) * mm, "end": v(258.87, 350) * mm});
            skCircle(sketch, "E3.4.7.36", {"center": v(230, 350) * mm, "radius": 20 * mm, "construction": true});
            skLineSegment(sketch, "E3.4.7.38", {"start": v(206.9, 349.93) * mm, "end": v(218.4, 369.96) * mm});
            skLineSegment(sketch, "E3.4.7.39", {"start": v(218.51, 329.96) * mm, "end": v(206.9, 349.93) * mm});
            skLineSegment(sketch, "E3.4.7.40", {"start": v(253.1, 350.07) * mm, "end": v(241.6, 330.04) * mm});
            skLineSegment(sketch, "E3.4.7.41", {"start": v(241.49, 370.04) * mm, "end": v(253.1, 350.07) * mm});
            skLineSegment(sketch, "E3.4.8.7", {"start": v(215.57, 375) * mm, "end": v(201.13, 400) * mm});
            skLineSegment(sketch, "E3.4.8.9", {"start": v(244.43, 375) * mm, "end": v(215.57, 375) * mm});
            skLineSegment(sketch, "E3.4.8.10", {"start": v(258.87, 400) * mm, "end": v(244.43, 375) * mm});
            skPoint(sketch, "E3.4.8.12", {"position": v(230, 425) * mm});
            skPoint(sketch, "E3.4.8.13", {"position": v(247.29, 410.05) * mm});
            skLineSegment(sketch, "E3.4.8.16", {"start": v(241.6, 380.04) * mm, "end": v(218.51, 379.96) * mm});
            skCircle(sketch, "E3.4.8.19", {"center": v(230, 400) * mm, "radius": 25 * mm, "construction": true});
            skLineSegment(sketch, "E3.4.8.20", {"start": v(215.57, 425) * mm, "end": v(244.43, 425) * mm});
            skLineSegment(sketch, "E3.4.8.23", {"start": v(218.4, 419.96) * mm, "end": v(241.49, 420.04) * mm});
            skLineSegment(sketch, "E3.4.8.28", {"start": v(201.13, 400) * mm, "end": v(215.57, 425) * mm});
            skLineSegment(sketch, "E3.4.8.31", {"start": v(244.43, 425) * mm, "end": v(258.87, 400) * mm});
            skCircle(sketch, "E3.4.8.36", {"center": v(230, 400) * mm, "radius": 20 * mm, "construction": true});
            skLineSegment(sketch, "E3.4.8.38", {"start": v(206.9, 399.93) * mm, "end": v(218.4, 419.96) * mm});
            skLineSegment(sketch, "E3.4.8.39", {"start": v(218.51, 379.96) * mm, "end": v(206.9, 399.93) * mm});
            skLineSegment(sketch, "E3.4.8.40", {"start": v(253.1, 400.07) * mm, "end": v(241.6, 380.04) * mm});
            skLineSegment(sketch, "E3.4.8.41", {"start": v(241.49, 420.04) * mm, "end": v(253.1, 400.07) * mm});
            skLineSegment(sketch, "E3.4.9.7", {"start": v(215.57, 425) * mm, "end": v(201.13, 450) * mm});
            skLineSegment(sketch, "E3.4.9.9", {"start": v(244.43, 425) * mm, "end": v(215.57, 425) * mm});
            skLineSegment(sketch, "E3.4.9.10", {"start": v(258.87, 450) * mm, "end": v(244.43, 425) * mm});
            skPoint(sketch, "E3.4.9.12", {"position": v(230, 475) * mm});
            skPoint(sketch, "E3.4.9.13", {"position": v(247.29, 460.05) * mm});
            skLineSegment(sketch, "E3.4.9.16", {"start": v(241.6, 430.04) * mm, "end": v(218.51, 429.96) * mm});
            skCircle(sketch, "E3.4.9.19", {"center": v(230, 450) * mm, "radius": 25 * mm, "construction": true});
            skLineSegment(sketch, "E3.4.9.20", {"start": v(215.57, 475) * mm, "end": v(244.43, 475) * mm});
            skLineSegment(sketch, "E3.4.9.23", {"start": v(218.4, 469.96) * mm, "end": v(241.49, 470.04) * mm});
            skLineSegment(sketch, "E3.4.9.28", {"start": v(201.13, 450) * mm, "end": v(215.57, 475) * mm});
            skLineSegment(sketch, "E3.4.9.31", {"start": v(244.43, 475) * mm, "end": v(258.87, 450) * mm});
            skCircle(sketch, "E3.4.9.36", {"center": v(230, 450) * mm, "radius": 20 * mm, "construction": true});
            skLineSegment(sketch, "E3.4.9.38", {"start": v(206.9, 449.93) * mm, "end": v(218.4, 469.96) * mm});
            skLineSegment(sketch, "E3.4.9.39", {"start": v(218.51, 429.96) * mm, "end": v(206.9, 449.93) * mm});
            skLineSegment(sketch, "E3.4.9.40", {"start": v(253.1, 450.07) * mm, "end": v(241.6, 430.04) * mm});
            skLineSegment(sketch, "E3.4.9.41", {"start": v(241.49, 470.04) * mm, "end": v(253.1, 450.07) * mm});
            skLineSegment(sketch, "E3.5.0.7", {"start": v(273.07, -25) * mm, "end": v(258.63, 0) * mm});
            skLineSegment(sketch, "E3.5.0.9", {"start": v(301.93, -25) * mm, "end": v(273.07, -25) * mm});
            skLineSegment(sketch, "E3.5.0.10", {"start": v(316.37, 0) * mm, "end": v(301.93, -25) * mm});
            skPoint(sketch, "E3.5.0.12", {"position": v(287.5, 25) * mm});
            skPoint(sketch, "E3.5.0.13", {"position": v(304.79, 10.05) * mm});
            skLineSegment(sketch, "E3.5.0.16", {"start": v(299.1, -19.96) * mm, "end": v(276.01, -20.04) * mm});
            skCircle(sketch, "E3.5.0.19", {"center": v(287.5, 0) * mm, "radius": 25 * mm, "construction": true});
            skLineSegment(sketch, "E3.5.0.20", {"start": v(273.07, 25) * mm, "end": v(301.93, 25) * mm});
            skLineSegment(sketch, "E3.5.0.23", {"start": v(275.9, 19.96) * mm, "end": v(298.99, 20.04) * mm});
            skLineSegment(sketch, "E3.5.0.28", {"start": v(258.63, 0) * mm, "end": v(273.07, 25) * mm});
            skLineSegment(sketch, "E3.5.0.31", {"start": v(301.93, 25) * mm, "end": v(316.37, 0) * mm});
            skCircle(sketch, "E3.5.0.36", {"center": v(287.5, 0) * mm, "radius": 20 * mm, "construction": true});
            skLineSegment(sketch, "E3.5.0.38", {"start": v(264.4, -0.07) * mm, "end": v(275.9, 19.96) * mm});
            skLineSegment(sketch, "E3.5.0.39", {"start": v(276.01, -20.04) * mm, "end": v(264.4, -0.07) * mm});
            skLineSegment(sketch, "E3.5.0.40", {"start": v(310.6, 0.07) * mm, "end": v(299.1, -19.96) * mm});
            skLineSegment(sketch, "E3.5.0.41", {"start": v(298.99, 20.04) * mm, "end": v(310.6, 0.07) * mm});
            skLineSegment(sketch, "E3.5.1.7", {"start": v(273.07, 25) * mm, "end": v(258.63, 50) * mm});
            skLineSegment(sketch, "E3.5.1.9", {"start": v(301.93, 25) * mm, "end": v(273.07, 25) * mm});
            skLineSegment(sketch, "E3.5.1.10", {"start": v(316.37, 50) * mm, "end": v(301.93, 25) * mm});
            skPoint(sketch, "E3.5.1.12", {"position": v(287.5, 75) * mm});
            skPoint(sketch, "E3.5.1.13", {"position": v(304.79, 60.05) * mm});
            skLineSegment(sketch, "E3.5.1.16", {"start": v(299.1, 30.04) * mm, "end": v(276.01, 29.96) * mm});
            skCircle(sketch, "E3.5.1.19", {"center": v(287.5, 50) * mm, "radius": 25 * mm, "construction": true});
            skLineSegment(sketch, "E3.5.1.20", {"start": v(273.07, 75) * mm, "end": v(301.93, 75) * mm});
            skLineSegment(sketch, "E3.5.1.23", {"start": v(275.9, 69.96) * mm, "end": v(298.99, 70.04) * mm});
            skLineSegment(sketch, "E3.5.1.28", {"start": v(258.63, 50) * mm, "end": v(273.07, 75) * mm});
            skLineSegment(sketch, "E3.5.1.31", {"start": v(301.93, 75) * mm, "end": v(316.37, 50) * mm});
            skCircle(sketch, "E3.5.1.36", {"center": v(287.5, 50) * mm, "radius": 20 * mm, "construction": true});
            skLineSegment(sketch, "E3.5.1.38", {"start": v(264.4, 49.93) * mm, "end": v(275.9, 69.96) * mm});
            skLineSegment(sketch, "E3.5.1.39", {"start": v(276.01, 29.96) * mm, "end": v(264.4, 49.93) * mm});
            skLineSegment(sketch, "E3.5.1.40", {"start": v(310.6, 50.07) * mm, "end": v(299.1, 30.04) * mm});
            skLineSegment(sketch, "E3.5.1.41", {"start": v(298.99, 70.04) * mm, "end": v(310.6, 50.07) * mm});
            skLineSegment(sketch, "E3.5.2.7", {"start": v(273.07, 75) * mm, "end": v(258.63, 100) * mm});
            skLineSegment(sketch, "E3.5.2.9", {"start": v(301.93, 75) * mm, "end": v(273.07, 75) * mm});
            skLineSegment(sketch, "E3.5.2.10", {"start": v(316.37, 100) * mm, "end": v(301.93, 75) * mm});
            skPoint(sketch, "E3.5.2.12", {"position": v(287.5, 125) * mm});
            skPoint(sketch, "E3.5.2.13", {"position": v(304.79, 110.05) * mm});
            skLineSegment(sketch, "E3.5.2.16", {"start": v(299.1, 80.04) * mm, "end": v(276.01, 79.96) * mm});
            skCircle(sketch, "E3.5.2.19", {"center": v(287.5, 100) * mm, "radius": 25 * mm, "construction": true});
            skLineSegment(sketch, "E3.5.2.20", {"start": v(273.07, 125) * mm, "end": v(301.93, 125) * mm});
            skLineSegment(sketch, "E3.5.2.23", {"start": v(275.9, 119.96) * mm, "end": v(298.99, 120.04) * mm});
            skLineSegment(sketch, "E3.5.2.28", {"start": v(258.63, 100) * mm, "end": v(273.07, 125) * mm});
            skLineSegment(sketch, "E3.5.2.31", {"start": v(301.93, 125) * mm, "end": v(316.37, 100) * mm});
            skCircle(sketch, "E3.5.2.36", {"center": v(287.5, 100) * mm, "radius": 20 * mm, "construction": true});
            skLineSegment(sketch, "E3.5.2.38", {"start": v(264.4, 99.93) * mm, "end": v(275.9, 119.96) * mm});
            skLineSegment(sketch, "E3.5.2.39", {"start": v(276.01, 79.96) * mm, "end": v(264.4, 99.93) * mm});
            skLineSegment(sketch, "E3.5.2.40", {"start": v(310.6, 100.07) * mm, "end": v(299.1, 80.04) * mm});
            skLineSegment(sketch, "E3.5.2.41", {"start": v(298.99, 120.04) * mm, "end": v(310.6, 100.07) * mm});
            skLineSegment(sketch, "E3.5.3.7", {"start": v(273.07, 125) * mm, "end": v(258.63, 150) * mm});
            skLineSegment(sketch, "E3.5.3.9", {"start": v(301.93, 125) * mm, "end": v(273.07, 125) * mm});
            skLineSegment(sketch, "E3.5.3.10", {"start": v(316.37, 150) * mm, "end": v(301.93, 125) * mm});
            skPoint(sketch, "E3.5.3.12", {"position": v(287.5, 175) * mm});
            skPoint(sketch, "E3.5.3.13", {"position": v(304.79, 160.05) * mm});
            skLineSegment(sketch, "E3.5.3.16", {"start": v(299.1, 130.04) * mm, "end": v(276.01, 129.96) * mm});
            skCircle(sketch, "E3.5.3.19", {"center": v(287.5, 150) * mm, "radius": 25 * mm, "construction": true});
            skLineSegment(sketch, "E3.5.3.20", {"start": v(273.07, 175) * mm, "end": v(301.93, 175) * mm});
            skLineSegment(sketch, "E3.5.3.23", {"start": v(275.9, 169.96) * mm, "end": v(298.99, 170.04) * mm});
            skLineSegment(sketch, "E3.5.3.28", {"start": v(258.63, 150) * mm, "end": v(273.07, 175) * mm});
            skLineSegment(sketch, "E3.5.3.31", {"start": v(301.93, 175) * mm, "end": v(316.37, 150) * mm});
            skCircle(sketch, "E3.5.3.36", {"center": v(287.5, 150) * mm, "radius": 20 * mm, "construction": true});
            skLineSegment(sketch, "E3.5.3.38", {"start": v(264.4, 149.93) * mm, "end": v(275.9, 169.96) * mm});
            skLineSegment(sketch, "E3.5.3.39", {"start": v(276.01, 129.96) * mm, "end": v(264.4, 149.93) * mm});
            skLineSegment(sketch, "E3.5.3.40", {"start": v(310.6, 150.07) * mm, "end": v(299.1, 130.04) * mm});
            skLineSegment(sketch, "E3.5.3.41", {"start": v(298.99, 170.04) * mm, "end": v(310.6, 150.07) * mm});
            skLineSegment(sketch, "E3.5.4.7", {"start": v(273.07, 175) * mm, "end": v(258.63, 200) * mm});
            skLineSegment(sketch, "E3.5.4.9", {"start": v(301.93, 175) * mm, "end": v(273.07, 175) * mm});
            skLineSegment(sketch, "E3.5.4.10", {"start": v(316.37, 200) * mm, "end": v(301.93, 175) * mm});
            skPoint(sketch, "E3.5.4.12", {"position": v(287.5, 225) * mm});
            skPoint(sketch, "E3.5.4.13", {"position": v(304.79, 210.05) * mm});
            skLineSegment(sketch, "E3.5.4.16", {"start": v(299.1, 180.04) * mm, "end": v(276.01, 179.96) * mm});
            skCircle(sketch, "E3.5.4.19", {"center": v(287.5, 200) * mm, "radius": 25 * mm, "construction": true});
            skLineSegment(sketch, "E3.5.4.20", {"start": v(273.07, 225) * mm, "end": v(301.93, 225) * mm});
            skLineSegment(sketch, "E3.5.4.23", {"start": v(275.9, 219.96) * mm, "end": v(298.99, 220.04) * mm});
            skLineSegment(sketch, "E3.5.4.28", {"start": v(258.63, 200) * mm, "end": v(273.07, 225) * mm});
            skLineSegment(sketch, "E3.5.4.31", {"start": v(301.93, 225) * mm, "end": v(316.37, 200) * mm});
            skCircle(sketch, "E3.5.4.36", {"center": v(287.5, 200) * mm, "radius": 20 * mm, "construction": true});
            skLineSegment(sketch, "E3.5.4.38", {"start": v(264.4, 199.93) * mm, "end": v(275.9, 219.96) * mm});
            skLineSegment(sketch, "E3.5.4.39", {"start": v(276.01, 179.96) * mm, "end": v(264.4, 199.93) * mm});
            skLineSegment(sketch, "E3.5.4.40", {"start": v(310.6, 200.07) * mm, "end": v(299.1, 180.04) * mm});
            skLineSegment(sketch, "E3.5.4.41", {"start": v(298.99, 220.04) * mm, "end": v(310.6, 200.07) * mm});
            skLineSegment(sketch, "E3.5.5.7", {"start": v(273.07, 225) * mm, "end": v(258.63, 250) * mm});
            skLineSegment(sketch, "E3.5.5.9", {"start": v(301.93, 225) * mm, "end": v(273.07, 225) * mm});
            skLineSegment(sketch, "E3.5.5.10", {"start": v(316.37, 250) * mm, "end": v(301.93, 225) * mm});
            skPoint(sketch, "E3.5.5.12", {"position": v(287.5, 275) * mm});
            skPoint(sketch, "E3.5.5.13", {"position": v(304.79, 260.05) * mm});
            skLineSegment(sketch, "E3.5.5.16", {"start": v(299.1, 230.04) * mm, "end": v(276.01, 229.96) * mm});
            skCircle(sketch, "E3.5.5.19", {"center": v(287.5, 250) * mm, "radius": 25 * mm, "construction": true});
            skLineSegment(sketch, "E3.5.5.20", {"start": v(273.07, 275) * mm, "end": v(301.93, 275) * mm});
            skLineSegment(sketch, "E3.5.5.23", {"start": v(275.9, 269.96) * mm, "end": v(298.99, 270.04) * mm});
            skLineSegment(sketch, "E3.5.5.28", {"start": v(258.63, 250) * mm, "end": v(273.07, 275) * mm});
            skLineSegment(sketch, "E3.5.5.31", {"start": v(301.93, 275) * mm, "end": v(316.37, 250) * mm});
            skCircle(sketch, "E3.5.5.36", {"center": v(287.5, 250) * mm, "radius": 20 * mm, "construction": true});
            skLineSegment(sketch, "E3.5.5.38", {"start": v(264.4, 249.93) * mm, "end": v(275.9, 269.96) * mm});
            skLineSegment(sketch, "E3.5.5.39", {"start": v(276.01, 229.96) * mm, "end": v(264.4, 249.93) * mm});
            skLineSegment(sketch, "E3.5.5.40", {"start": v(310.6, 250.07) * mm, "end": v(299.1, 230.04) * mm});
            skLineSegment(sketch, "E3.5.5.41", {"start": v(298.99, 270.04) * mm, "end": v(310.6, 250.07) * mm});
            skLineSegment(sketch, "E3.5.6.7", {"start": v(273.07, 275) * mm, "end": v(258.63, 300) * mm});
            skLineSegment(sketch, "E3.5.6.9", {"start": v(301.93, 275) * mm, "end": v(273.07, 275) * mm});
            skLineSegment(sketch, "E3.5.6.10", {"start": v(316.37, 300) * mm, "end": v(301.93, 275) * mm});
            skPoint(sketch, "E3.5.6.12", {"position": v(287.5, 325) * mm});
            skPoint(sketch, "E3.5.6.13", {"position": v(304.79, 310.05) * mm});
            skLineSegment(sketch, "E3.5.6.16", {"start": v(299.1, 280.04) * mm, "end": v(276.01, 279.96) * mm});
            skCircle(sketch, "E3.5.6.19", {"center": v(287.5, 300) * mm, "radius": 25 * mm, "construction": true});
            skLineSegment(sketch, "E3.5.6.20", {"start": v(273.07, 325) * mm, "end": v(301.93, 325) * mm});
            skLineSegment(sketch, "E3.5.6.23", {"start": v(275.9, 319.96) * mm, "end": v(298.99, 320.04) * mm});
            skLineSegment(sketch, "E3.5.6.28", {"start": v(258.63, 300) * mm, "end": v(273.07, 325) * mm});
            skLineSegment(sketch, "E3.5.6.31", {"start": v(301.93, 325) * mm, "end": v(316.37, 300) * mm});
            skCircle(sketch, "E3.5.6.36", {"center": v(287.5, 300) * mm, "radius": 20 * mm, "construction": true});
            skLineSegment(sketch, "E3.5.6.38", {"start": v(264.4, 299.93) * mm, "end": v(275.9, 319.96) * mm});
            skLineSegment(sketch, "E3.5.6.39", {"start": v(276.01, 279.96) * mm, "end": v(264.4, 299.93) * mm});
            skLineSegment(sketch, "E3.5.6.40", {"start": v(310.6, 300.07) * mm, "end": v(299.1, 280.04) * mm});
            skLineSegment(sketch, "E3.5.6.41", {"start": v(298.99, 320.04) * mm, "end": v(310.6, 300.07) * mm});
            skLineSegment(sketch, "E3.5.7.7", {"start": v(273.07, 325) * mm, "end": v(258.63, 350) * mm});
            skLineSegment(sketch, "E3.5.7.9", {"start": v(301.93, 325) * mm, "end": v(273.07, 325) * mm});
            skLineSegment(sketch, "E3.5.7.10", {"start": v(316.37, 350) * mm, "end": v(301.93, 325) * mm});
            skPoint(sketch, "E3.5.7.12", {"position": v(287.5, 375) * mm});
            skPoint(sketch, "E3.5.7.13", {"position": v(304.79, 360.05) * mm});
            skLineSegment(sketch, "E3.5.7.16", {"start": v(299.1, 330.04) * mm, "end": v(276.01, 329.96) * mm});
            skCircle(sketch, "E3.5.7.19", {"center": v(287.5, 350) * mm, "radius": 25 * mm, "construction": true});
            skLineSegment(sketch, "E3.5.7.20", {"start": v(273.07, 375) * mm, "end": v(301.93, 375) * mm});
            skLineSegment(sketch, "E3.5.7.23", {"start": v(275.9, 369.96) * mm, "end": v(298.99, 370.04) * mm});
            skLineSegment(sketch, "E3.5.7.28", {"start": v(258.63, 350) * mm, "end": v(273.07, 375) * mm});
            skLineSegment(sketch, "E3.5.7.31", {"start": v(301.93, 375) * mm, "end": v(316.37, 350) * mm});
            skCircle(sketch, "E3.5.7.36", {"center": v(287.5, 350) * mm, "radius": 20 * mm, "construction": true});
            skLineSegment(sketch, "E3.5.7.38", {"start": v(264.4, 349.93) * mm, "end": v(275.9, 369.96) * mm});
            skLineSegment(sketch, "E3.5.7.39", {"start": v(276.01, 329.96) * mm, "end": v(264.4, 349.93) * mm});
            skLineSegment(sketch, "E3.5.7.40", {"start": v(310.6, 350.07) * mm, "end": v(299.1, 330.04) * mm});
            skLineSegment(sketch, "E3.5.7.41", {"start": v(298.99, 370.04) * mm, "end": v(310.6, 350.07) * mm});
            skLineSegment(sketch, "E3.5.8.7", {"start": v(273.07, 375) * mm, "end": v(258.63, 400) * mm});
            skLineSegment(sketch, "E3.5.8.9", {"start": v(301.93, 375) * mm, "end": v(273.07, 375) * mm});
            skLineSegment(sketch, "E3.5.8.10", {"start": v(316.37, 400) * mm, "end": v(301.93, 375) * mm});
            skPoint(sketch, "E3.5.8.12", {"position": v(287.5, 425) * mm});
            skPoint(sketch, "E3.5.8.13", {"position": v(304.79, 410.05) * mm});
            skLineSegment(sketch, "E3.5.8.16", {"start": v(299.1, 380.04) * mm, "end": v(276.01, 379.96) * mm});
            skCircle(sketch, "E3.5.8.19", {"center": v(287.5, 400) * mm, "radius": 25 * mm, "construction": true});
            skLineSegment(sketch, "E3.5.8.20", {"start": v(273.07, 425) * mm, "end": v(301.93, 425) * mm});
            skLineSegment(sketch, "E3.5.8.23", {"start": v(275.9, 419.96) * mm, "end": v(298.99, 420.04) * mm});
            skLineSegment(sketch, "E3.5.8.28", {"start": v(258.63, 400) * mm, "end": v(273.07, 425) * mm});
            skLineSegment(sketch, "E3.5.8.31", {"start": v(301.93, 425) * mm, "end": v(316.37, 400) * mm});
            skCircle(sketch, "E3.5.8.36", {"center": v(287.5, 400) * mm, "radius": 20 * mm, "construction": true});
            skLineSegment(sketch, "E3.5.8.38", {"start": v(264.4, 399.93) * mm, "end": v(275.9, 419.96) * mm});
            skLineSegment(sketch, "E3.5.8.39", {"start": v(276.01, 379.96) * mm, "end": v(264.4, 399.93) * mm});
            skLineSegment(sketch, "E3.5.8.40", {"start": v(310.6, 400.07) * mm, "end": v(299.1, 380.04) * mm});
            skLineSegment(sketch, "E3.5.8.41", {"start": v(298.99, 420.04) * mm, "end": v(310.6, 400.07) * mm});
            skLineSegment(sketch, "E3.5.9.7", {"start": v(273.07, 425) * mm, "end": v(258.63, 450) * mm});
            skLineSegment(sketch, "E3.5.9.9", {"start": v(301.93, 425) * mm, "end": v(273.07, 425) * mm});
            skLineSegment(sketch, "E3.5.9.10", {"start": v(316.37, 450) * mm, "end": v(301.93, 425) * mm});
            skPoint(sketch, "E3.5.9.12", {"position": v(287.5, 475) * mm});
            skPoint(sketch, "E3.5.9.13", {"position": v(304.79, 460.05) * mm});
            skLineSegment(sketch, "E3.5.9.16", {"start": v(299.1, 430.04) * mm, "end": v(276.01, 429.96) * mm});
            skCircle(sketch, "E3.5.9.19", {"center": v(287.5, 450) * mm, "radius": 25 * mm, "construction": true});
            skLineSegment(sketch, "E3.5.9.20", {"start": v(273.07, 475) * mm, "end": v(301.93, 475) * mm});
            skLineSegment(sketch, "E3.5.9.23", {"start": v(275.9, 469.96) * mm, "end": v(298.99, 470.04) * mm});
            skLineSegment(sketch, "E3.5.9.28", {"start": v(258.63, 450) * mm, "end": v(273.07, 475) * mm});
            skLineSegment(sketch, "E3.5.9.31", {"start": v(301.93, 475) * mm, "end": v(316.37, 450) * mm});
            skCircle(sketch, "E3.5.9.36", {"center": v(287.5, 450) * mm, "radius": 20 * mm, "construction": true});
            skLineSegment(sketch, "E3.5.9.38", {"start": v(264.4, 449.93) * mm, "end": v(275.9, 469.96) * mm});
            skLineSegment(sketch, "E3.5.9.39", {"start": v(276.01, 429.96) * mm, "end": v(264.4, 449.93) * mm});
            skLineSegment(sketch, "E3.5.9.40", {"start": v(310.6, 450.07) * mm, "end": v(299.1, 430.04) * mm});
            skLineSegment(sketch, "E3.5.9.41", {"start": v(298.99, 470.04) * mm, "end": v(310.6, 450.07) * mm});
            skLineSegment(sketch, "E3.6.0.7", {"start": v(330.57, -25) * mm, "end": v(316.13, 0) * mm});
            skLineSegment(sketch, "E3.6.0.9", {"start": v(359.43, -25) * mm, "end": v(330.57, -25) * mm});
            skLineSegment(sketch, "E3.6.0.10", {"start": v(373.87, 0) * mm, "end": v(359.43, -25) * mm});
            skPoint(sketch, "E3.6.0.12", {"position": v(345, 25) * mm});
            skPoint(sketch, "E3.6.0.13", {"position": v(362.29, 10.05) * mm});
            skLineSegment(sketch, "E3.6.0.16", {"start": v(356.6, -19.96) * mm, "end": v(333.51, -20.04) * mm});
            skCircle(sketch, "E3.6.0.19", {"center": v(345, 0) * mm, "radius": 25 * mm, "construction": true});
            skLineSegment(sketch, "E3.6.0.20", {"start": v(330.57, 25) * mm, "end": v(359.43, 25) * mm});
            skLineSegment(sketch, "E3.6.0.23", {"start": v(333.4, 19.96) * mm, "end": v(356.49, 20.04) * mm});
            skLineSegment(sketch, "E3.6.0.28", {"start": v(316.13, 0) * mm, "end": v(330.57, 25) * mm});
            skLineSegment(sketch, "E3.6.0.31", {"start": v(359.43, 25) * mm, "end": v(373.87, 0) * mm});
            skCircle(sketch, "E3.6.0.36", {"center": v(345, 0) * mm, "radius": 20 * mm, "construction": true});
            skLineSegment(sketch, "E3.6.0.38", {"start": v(321.9, -0.07) * mm, "end": v(333.4, 19.96) * mm});
            skLineSegment(sketch, "E3.6.0.39", {"start": v(333.51, -20.04) * mm, "end": v(321.9, -0.07) * mm});
            skLineSegment(sketch, "E3.6.0.40", {"start": v(368.1, 0.07) * mm, "end": v(356.6, -19.96) * mm});
            skLineSegment(sketch, "E3.6.0.41", {"start": v(356.49, 20.04) * mm, "end": v(368.1, 0.07) * mm});
            skLineSegment(sketch, "E3.6.1.7", {"start": v(330.57, 25) * mm, "end": v(316.13, 50) * mm});
            skLineSegment(sketch, "E3.6.1.9", {"start": v(359.43, 25) * mm, "end": v(330.57, 25) * mm});
            skLineSegment(sketch, "E3.6.1.10", {"start": v(373.87, 50) * mm, "end": v(359.43, 25) * mm});
            skPoint(sketch, "E3.6.1.12", {"position": v(345, 75) * mm});
            skPoint(sketch, "E3.6.1.13", {"position": v(362.29, 60.05) * mm});
            skLineSegment(sketch, "E3.6.1.16", {"start": v(356.6, 30.04) * mm, "end": v(333.51, 29.96) * mm});
            skCircle(sketch, "E3.6.1.19", {"center": v(345, 50) * mm, "radius": 25 * mm, "construction": true});
            skLineSegment(sketch, "E3.6.1.20", {"start": v(330.57, 75) * mm, "end": v(359.43, 75) * mm});
            skLineSegment(sketch, "E3.6.1.23", {"start": v(333.4, 69.96) * mm, "end": v(356.49, 70.04) * mm});
            skLineSegment(sketch, "E3.6.1.28", {"start": v(316.13, 50) * mm, "end": v(330.57, 75) * mm});
            skLineSegment(sketch, "E3.6.1.31", {"start": v(359.43, 75) * mm, "end": v(373.87, 50) * mm});
            skCircle(sketch, "E3.6.1.36", {"center": v(345, 50) * mm, "radius": 20 * mm, "construction": true});
            skLineSegment(sketch, "E3.6.1.38", {"start": v(321.9, 49.93) * mm, "end": v(333.4, 69.96) * mm});
            skLineSegment(sketch, "E3.6.1.39", {"start": v(333.51, 29.96) * mm, "end": v(321.9, 49.93) * mm});
            skLineSegment(sketch, "E3.6.1.40", {"start": v(368.1, 50.07) * mm, "end": v(356.6, 30.04) * mm});
            skLineSegment(sketch, "E3.6.1.41", {"start": v(356.49, 70.04) * mm, "end": v(368.1, 50.07) * mm});
            skLineSegment(sketch, "E3.6.2.7", {"start": v(330.57, 75) * mm, "end": v(316.13, 100) * mm});
            skLineSegment(sketch, "E3.6.2.9", {"start": v(359.43, 75) * mm, "end": v(330.57, 75) * mm});
            skLineSegment(sketch, "E3.6.2.10", {"start": v(373.87, 100) * mm, "end": v(359.43, 75) * mm});
            skPoint(sketch, "E3.6.2.12", {"position": v(345, 125) * mm});
            skPoint(sketch, "E3.6.2.13", {"position": v(362.29, 110.05) * mm});
            skLineSegment(sketch, "E3.6.2.16", {"start": v(356.6, 80.04) * mm, "end": v(333.51, 79.96) * mm});
            skCircle(sketch, "E3.6.2.19", {"center": v(345, 100) * mm, "radius": 25 * mm, "construction": true});
            skLineSegment(sketch, "E3.6.2.20", {"start": v(330.57, 125) * mm, "end": v(359.43, 125) * mm});
            skLineSegment(sketch, "E3.6.2.23", {"start": v(333.4, 119.96) * mm, "end": v(356.49, 120.04) * mm});
            skLineSegment(sketch, "E3.6.2.28", {"start": v(316.13, 100) * mm, "end": v(330.57, 125) * mm});
            skLineSegment(sketch, "E3.6.2.31", {"start": v(359.43, 125) * mm, "end": v(373.87, 100) * mm});
            skCircle(sketch, "E3.6.2.36", {"center": v(345, 100) * mm, "radius": 20 * mm, "construction": true});
            skLineSegment(sketch, "E3.6.2.38", {"start": v(321.9, 99.93) * mm, "end": v(333.4, 119.96) * mm});
            skLineSegment(sketch, "E3.6.2.39", {"start": v(333.51, 79.96) * mm, "end": v(321.9, 99.93) * mm});
            skLineSegment(sketch, "E3.6.2.40", {"start": v(368.1, 100.07) * mm, "end": v(356.6, 80.04) * mm});
            skLineSegment(sketch, "E3.6.2.41", {"start": v(356.49, 120.04) * mm, "end": v(368.1, 100.07) * mm});
            skLineSegment(sketch, "E3.6.3.7", {"start": v(330.57, 125) * mm, "end": v(316.13, 150) * mm});
            skLineSegment(sketch, "E3.6.3.9", {"start": v(359.43, 125) * mm, "end": v(330.57, 125) * mm});
            skLineSegment(sketch, "E3.6.3.10", {"start": v(373.87, 150) * mm, "end": v(359.43, 125) * mm});
            skPoint(sketch, "E3.6.3.12", {"position": v(345, 175) * mm});
            skPoint(sketch, "E3.6.3.13", {"position": v(362.29, 160.05) * mm});
            skLineSegment(sketch, "E3.6.3.16", {"start": v(356.6, 130.04) * mm, "end": v(333.51, 129.96) * mm});
            skCircle(sketch, "E3.6.3.19", {"center": v(345, 150) * mm, "radius": 25 * mm, "construction": true});
            skLineSegment(sketch, "E3.6.3.20", {"start": v(330.57, 175) * mm, "end": v(359.43, 175) * mm});
            skLineSegment(sketch, "E3.6.3.23", {"start": v(333.4, 169.96) * mm, "end": v(356.49, 170.04) * mm});
            skLineSegment(sketch, "E3.6.3.28", {"start": v(316.13, 150) * mm, "end": v(330.57, 175) * mm});
            skLineSegment(sketch, "E3.6.3.31", {"start": v(359.43, 175) * mm, "end": v(373.87, 150) * mm});
            skCircle(sketch, "E3.6.3.36", {"center": v(345, 150) * mm, "radius": 20 * mm, "construction": true});
            skLineSegment(sketch, "E3.6.3.38", {"start": v(321.9, 149.93) * mm, "end": v(333.4, 169.96) * mm});
            skLineSegment(sketch, "E3.6.3.39", {"start": v(333.51, 129.96) * mm, "end": v(321.9, 149.93) * mm});
            skLineSegment(sketch, "E3.6.3.40", {"start": v(368.1, 150.07) * mm, "end": v(356.6, 130.04) * mm});
            skLineSegment(sketch, "E3.6.3.41", {"start": v(356.49, 170.04) * mm, "end": v(368.1, 150.07) * mm});
            skLineSegment(sketch, "E3.6.4.7", {"start": v(330.57, 175) * mm, "end": v(316.13, 200) * mm});
            skLineSegment(sketch, "E3.6.4.9", {"start": v(359.43, 175) * mm, "end": v(330.57, 175) * mm});
            skLineSegment(sketch, "E3.6.4.10", {"start": v(373.87, 200) * mm, "end": v(359.43, 175) * mm});
            skPoint(sketch, "E3.6.4.12", {"position": v(345, 225) * mm});
            skPoint(sketch, "E3.6.4.13", {"position": v(362.29, 210.05) * mm});
            skLineSegment(sketch, "E3.6.4.16", {"start": v(356.6, 180.04) * mm, "end": v(333.51, 179.96) * mm});
            skCircle(sketch, "E3.6.4.19", {"center": v(345, 200) * mm, "radius": 25 * mm, "construction": true});
            skLineSegment(sketch, "E3.6.4.20", {"start": v(330.57, 225) * mm, "end": v(359.43, 225) * mm});
            skLineSegment(sketch, "E3.6.4.23", {"start": v(333.4, 219.96) * mm, "end": v(356.49, 220.04) * mm});
            skLineSegment(sketch, "E3.6.4.28", {"start": v(316.13, 200) * mm, "end": v(330.57, 225) * mm});
            skLineSegment(sketch, "E3.6.4.31", {"start": v(359.43, 225) * mm, "end": v(373.87, 200) * mm});
            skCircle(sketch, "E3.6.4.36", {"center": v(345, 200) * mm, "radius": 20 * mm, "construction": true});
            skLineSegment(sketch, "E3.6.4.38", {"start": v(321.9, 199.93) * mm, "end": v(333.4, 219.96) * mm});
            skLineSegment(sketch, "E3.6.4.39", {"start": v(333.51, 179.96) * mm, "end": v(321.9, 199.93) * mm});
            skLineSegment(sketch, "E3.6.4.40", {"start": v(368.1, 200.07) * mm, "end": v(356.6, 180.04) * mm});
            skLineSegment(sketch, "E3.6.4.41", {"start": v(356.49, 220.04) * mm, "end": v(368.1, 200.07) * mm});
            skLineSegment(sketch, "E3.6.5.7", {"start": v(330.57, 225) * mm, "end": v(316.13, 250) * mm});
            skLineSegment(sketch, "E3.6.5.9", {"start": v(359.43, 225) * mm, "end": v(330.57, 225) * mm});
            skLineSegment(sketch, "E3.6.5.10", {"start": v(373.87, 250) * mm, "end": v(359.43, 225) * mm});
            skPoint(sketch, "E3.6.5.12", {"position": v(345, 275) * mm});
            skPoint(sketch, "E3.6.5.13", {"position": v(362.29, 260.05) * mm});
            skLineSegment(sketch, "E3.6.5.16", {"start": v(356.6, 230.04) * mm, "end": v(333.51, 229.96) * mm});
            skCircle(sketch, "E3.6.5.19", {"center": v(345, 250) * mm, "radius": 25 * mm, "construction": true});
            skLineSegment(sketch, "E3.6.5.20", {"start": v(330.57, 275) * mm, "end": v(359.43, 275) * mm});
            skLineSegment(sketch, "E3.6.5.23", {"start": v(333.4, 269.96) * mm, "end": v(356.49, 270.04) * mm});
            skLineSegment(sketch, "E3.6.5.28", {"start": v(316.13, 250) * mm, "end": v(330.57, 275) * mm});
            skLineSegment(sketch, "E3.6.5.31", {"start": v(359.43, 275) * mm, "end": v(373.87, 250) * mm});
            skCircle(sketch, "E3.6.5.36", {"center": v(345, 250) * mm, "radius": 20 * mm, "construction": true});
            skLineSegment(sketch, "E3.6.5.38", {"start": v(321.9, 249.93) * mm, "end": v(333.4, 269.96) * mm});
            skLineSegment(sketch, "E3.6.5.39", {"start": v(333.51, 229.96) * mm, "end": v(321.9, 249.93) * mm});
            skLineSegment(sketch, "E3.6.5.40", {"start": v(368.1, 250.07) * mm, "end": v(356.6, 230.04) * mm});
            skLineSegment(sketch, "E3.6.5.41", {"start": v(356.49, 270.04) * mm, "end": v(368.1, 250.07) * mm});
            skLineSegment(sketch, "E3.6.6.7", {"start": v(330.57, 275) * mm, "end": v(316.13, 300) * mm});
            skLineSegment(sketch, "E3.6.6.9", {"start": v(359.43, 275) * mm, "end": v(330.57, 275) * mm});
            skLineSegment(sketch, "E3.6.6.10", {"start": v(373.87, 300) * mm, "end": v(359.43, 275) * mm});
            skPoint(sketch, "E3.6.6.12", {"position": v(345, 325) * mm});
            skPoint(sketch, "E3.6.6.13", {"position": v(362.29, 310.05) * mm});
            skLineSegment(sketch, "E3.6.6.16", {"start": v(356.6, 280.04) * mm, "end": v(333.51, 279.96) * mm});
            skCircle(sketch, "E3.6.6.19", {"center": v(345, 300) * mm, "radius": 25 * mm, "construction": true});
            skLineSegment(sketch, "E3.6.6.20", {"start": v(330.57, 325) * mm, "end": v(359.43, 325) * mm});
            skLineSegment(sketch, "E3.6.6.23", {"start": v(333.4, 319.96) * mm, "end": v(356.49, 320.04) * mm});
            skLineSegment(sketch, "E3.6.6.28", {"start": v(316.13, 300) * mm, "end": v(330.57, 325) * mm});
            skLineSegment(sketch, "E3.6.6.31", {"start": v(359.43, 325) * mm, "end": v(373.87, 300) * mm});
            skCircle(sketch, "E3.6.6.36", {"center": v(345, 300) * mm, "radius": 20 * mm, "construction": true});
            skLineSegment(sketch, "E3.6.6.38", {"start": v(321.9, 299.93) * mm, "end": v(333.4, 319.96) * mm});
            skLineSegment(sketch, "E3.6.6.39", {"start": v(333.51, 279.96) * mm, "end": v(321.9, 299.93) * mm});
            skLineSegment(sketch, "E3.6.6.40", {"start": v(368.1, 300.07) * mm, "end": v(356.6, 280.04) * mm});
            skLineSegment(sketch, "E3.6.6.41", {"start": v(356.49, 320.04) * mm, "end": v(368.1, 300.07) * mm});
            skLineSegment(sketch, "E3.6.7.7", {"start": v(330.57, 325) * mm, "end": v(316.13, 350) * mm});
            skLineSegment(sketch, "E3.6.7.9", {"start": v(359.43, 325) * mm, "end": v(330.57, 325) * mm});
            skLineSegment(sketch, "E3.6.7.10", {"start": v(373.87, 350) * mm, "end": v(359.43, 325) * mm});
            skPoint(sketch, "E3.6.7.12", {"position": v(345, 375) * mm});
            skPoint(sketch, "E3.6.7.13", {"position": v(362.29, 360.05) * mm});
            skLineSegment(sketch, "E3.6.7.16", {"start": v(356.6, 330.04) * mm, "end": v(333.51, 329.96) * mm});
            skCircle(sketch, "E3.6.7.19", {"center": v(345, 350) * mm, "radius": 25 * mm, "construction": true});
            skLineSegment(sketch, "E3.6.7.20", {"start": v(330.57, 375) * mm, "end": v(359.43, 375) * mm});
            skLineSegment(sketch, "E3.6.7.23", {"start": v(333.4, 369.96) * mm, "end": v(356.49, 370.04) * mm});
            skLineSegment(sketch, "E3.6.7.28", {"start": v(316.13, 350) * mm, "end": v(330.57, 375) * mm});
            skLineSegment(sketch, "E3.6.7.31", {"start": v(359.43, 375) * mm, "end": v(373.87, 350) * mm});
            skCircle(sketch, "E3.6.7.36", {"center": v(345, 350) * mm, "radius": 20 * mm, "construction": true});
            skLineSegment(sketch, "E3.6.7.38", {"start": v(321.9, 349.93) * mm, "end": v(333.4, 369.96) * mm});
            skLineSegment(sketch, "E3.6.7.39", {"start": v(333.51, 329.96) * mm, "end": v(321.9, 349.93) * mm});
            skLineSegment(sketch, "E3.6.7.40", {"start": v(368.1, 350.07) * mm, "end": v(356.6, 330.04) * mm});
            skLineSegment(sketch, "E3.6.7.41", {"start": v(356.49, 370.04) * mm, "end": v(368.1, 350.07) * mm});
            skLineSegment(sketch, "E3.6.8.7", {"start": v(330.57, 375) * mm, "end": v(316.13, 400) * mm});
            skLineSegment(sketch, "E3.6.8.9", {"start": v(359.43, 375) * mm, "end": v(330.57, 375) * mm});
            skLineSegment(sketch, "E3.6.8.10", {"start": v(373.87, 400) * mm, "end": v(359.43, 375) * mm});
            skPoint(sketch, "E3.6.8.12", {"position": v(345, 425) * mm});
            skPoint(sketch, "E3.6.8.13", {"position": v(362.29, 410.05) * mm});
            skLineSegment(sketch, "E3.6.8.16", {"start": v(356.6, 380.04) * mm, "end": v(333.51, 379.96) * mm});
            skCircle(sketch, "E3.6.8.19", {"center": v(345, 400) * mm, "radius": 25 * mm, "construction": true});
            skLineSegment(sketch, "E3.6.8.20", {"start": v(330.57, 425) * mm, "end": v(359.43, 425) * mm});
            skLineSegment(sketch, "E3.6.8.23", {"start": v(333.4, 419.96) * mm, "end": v(356.49, 420.04) * mm});
            skLineSegment(sketch, "E3.6.8.28", {"start": v(316.13, 400) * mm, "end": v(330.57, 425) * mm});
            skLineSegment(sketch, "E3.6.8.31", {"start": v(359.43, 425) * mm, "end": v(373.87, 400) * mm});
            skCircle(sketch, "E3.6.8.36", {"center": v(345, 400) * mm, "radius": 20 * mm, "construction": true});
            skLineSegment(sketch, "E3.6.8.38", {"start": v(321.9, 399.93) * mm, "end": v(333.4, 419.96) * mm});
            skLineSegment(sketch, "E3.6.8.39", {"start": v(333.51, 379.96) * mm, "end": v(321.9, 399.93) * mm});
            skLineSegment(sketch, "E3.6.8.40", {"start": v(368.1, 400.07) * mm, "end": v(356.6, 380.04) * mm});
            skLineSegment(sketch, "E3.6.8.41", {"start": v(356.49, 420.04) * mm, "end": v(368.1, 400.07) * mm});
            skLineSegment(sketch, "E3.6.9.7", {"start": v(330.57, 425) * mm, "end": v(316.13, 450) * mm});
            skLineSegment(sketch, "E3.6.9.9", {"start": v(359.43, 425) * mm, "end": v(330.57, 425) * mm});
            skLineSegment(sketch, "E3.6.9.10", {"start": v(373.87, 450) * mm, "end": v(359.43, 425) * mm});
            skPoint(sketch, "E3.6.9.12", {"position": v(345, 475) * mm});
            skPoint(sketch, "E3.6.9.13", {"position": v(362.29, 460.05) * mm});
            skLineSegment(sketch, "E3.6.9.16", {"start": v(356.6, 430.04) * mm, "end": v(333.51, 429.96) * mm});
            skCircle(sketch, "E3.6.9.19", {"center": v(345, 450) * mm, "radius": 25 * mm, "construction": true});
            skLineSegment(sketch, "E3.6.9.20", {"start": v(330.57, 475) * mm, "end": v(359.43, 475) * mm});
            skLineSegment(sketch, "E3.6.9.23", {"start": v(333.4, 469.96) * mm, "end": v(356.49, 470.04) * mm});
            skLineSegment(sketch, "E3.6.9.28", {"start": v(316.13, 450) * mm, "end": v(330.57, 475) * mm});
            skLineSegment(sketch, "E3.6.9.31", {"start": v(359.43, 475) * mm, "end": v(373.87, 450) * mm});
            skCircle(sketch, "E3.6.9.36", {"center": v(345, 450) * mm, "radius": 20 * mm, "construction": true});
            skLineSegment(sketch, "E3.6.9.38", {"start": v(321.9, 449.93) * mm, "end": v(333.4, 469.96) * mm});
            skLineSegment(sketch, "E3.6.9.39", {"start": v(333.51, 429.96) * mm, "end": v(321.9, 449.93) * mm});
            skLineSegment(sketch, "E3.6.9.40", {"start": v(368.1, 450.07) * mm, "end": v(356.6, 430.04) * mm});
            skLineSegment(sketch, "E3.6.9.41", {"start": v(356.49, 470.04) * mm, "end": v(368.1, 450.07) * mm});
            skLineSegment(sketch, "E3.7.0.7", {"start": v(388.07, -25) * mm, "end": v(373.63, 0) * mm});
            skLineSegment(sketch, "E3.7.0.9", {"start": v(416.93, -25) * mm, "end": v(388.07, -25) * mm});
            skLineSegment(sketch, "E3.7.0.10", {"start": v(431.37, 0) * mm, "end": v(416.93, -25) * mm});
            skPoint(sketch, "E3.7.0.12", {"position": v(402.5, 25) * mm});
            skPoint(sketch, "E3.7.0.13", {"position": v(419.79, 10.05) * mm});
            skLineSegment(sketch, "E3.7.0.16", {"start": v(414.1, -19.96) * mm, "end": v(391.01, -20.04) * mm});
            skCircle(sketch, "E3.7.0.19", {"center": v(402.5, 0) * mm, "radius": 25 * mm, "construction": true});
            skLineSegment(sketch, "E3.7.0.20", {"start": v(388.07, 25) * mm, "end": v(416.93, 25) * mm});
            skLineSegment(sketch, "E3.7.0.23", {"start": v(390.9, 19.96) * mm, "end": v(413.99, 20.04) * mm});
            skLineSegment(sketch, "E3.7.0.28", {"start": v(373.63, 0) * mm, "end": v(388.07, 25) * mm});
            skLineSegment(sketch, "E3.7.0.31", {"start": v(416.93, 25) * mm, "end": v(431.37, 0) * mm});
            skCircle(sketch, "E3.7.0.36", {"center": v(402.5, 0) * mm, "radius": 20 * mm, "construction": true});
            skLineSegment(sketch, "E3.7.0.38", {"start": v(379.4, -0.07) * mm, "end": v(390.9, 19.96) * mm});
            skLineSegment(sketch, "E3.7.0.39", {"start": v(391.01, -20.04) * mm, "end": v(379.4, -0.07) * mm});
            skLineSegment(sketch, "E3.7.0.40", {"start": v(425.6, 0.07) * mm, "end": v(414.1, -19.96) * mm});
            skLineSegment(sketch, "E3.7.0.41", {"start": v(413.99, 20.04) * mm, "end": v(425.6, 0.07) * mm});
            skLineSegment(sketch, "E3.7.1.7", {"start": v(388.07, 25) * mm, "end": v(373.63, 50) * mm});
            skLineSegment(sketch, "E3.7.1.9", {"start": v(416.93, 25) * mm, "end": v(388.07, 25) * mm});
            skLineSegment(sketch, "E3.7.1.10", {"start": v(431.37, 50) * mm, "end": v(416.93, 25) * mm});
            skPoint(sketch, "E3.7.1.12", {"position": v(402.5, 75) * mm});
            skPoint(sketch, "E3.7.1.13", {"position": v(419.79, 60.05) * mm});
            skLineSegment(sketch, "E3.7.1.16", {"start": v(414.1, 30.04) * mm, "end": v(391.01, 29.96) * mm});
            skCircle(sketch, "E3.7.1.19", {"center": v(402.5, 50) * mm, "radius": 25 * mm, "construction": true});
            skLineSegment(sketch, "E3.7.1.20", {"start": v(388.07, 75) * mm, "end": v(416.93, 75) * mm});
            skLineSegment(sketch, "E3.7.1.23", {"start": v(390.9, 69.96) * mm, "end": v(413.99, 70.04) * mm});
            skLineSegment(sketch, "E3.7.1.28", {"start": v(373.63, 50) * mm, "end": v(388.07, 75) * mm});
            skLineSegment(sketch, "E3.7.1.31", {"start": v(416.93, 75) * mm, "end": v(431.37, 50) * mm});
            skCircle(sketch, "E3.7.1.36", {"center": v(402.5, 50) * mm, "radius": 20 * mm, "construction": true});
            skLineSegment(sketch, "E3.7.1.38", {"start": v(379.4, 49.93) * mm, "end": v(390.9, 69.96) * mm});
            skLineSegment(sketch, "E3.7.1.39", {"start": v(391.01, 29.96) * mm, "end": v(379.4, 49.93) * mm});
            skLineSegment(sketch, "E3.7.1.40", {"start": v(425.6, 50.07) * mm, "end": v(414.1, 30.04) * mm});
            skLineSegment(sketch, "E3.7.1.41", {"start": v(413.99, 70.04) * mm, "end": v(425.6, 50.07) * mm});
            skLineSegment(sketch, "E3.7.2.7", {"start": v(388.07, 75) * mm, "end": v(373.63, 100) * mm});
            skLineSegment(sketch, "E3.7.2.9", {"start": v(416.93, 75) * mm, "end": v(388.07, 75) * mm});
            skLineSegment(sketch, "E3.7.2.10", {"start": v(431.37, 100) * mm, "end": v(416.93, 75) * mm});
            skPoint(sketch, "E3.7.2.12", {"position": v(402.5, 125) * mm});
            skPoint(sketch, "E3.7.2.13", {"position": v(419.79, 110.05) * mm});
            skLineSegment(sketch, "E3.7.2.16", {"start": v(414.1, 80.04) * mm, "end": v(391.01, 79.96) * mm});
            skCircle(sketch, "E3.7.2.19", {"center": v(402.5, 100) * mm, "radius": 25 * mm, "construction": true});
            skLineSegment(sketch, "E3.7.2.20", {"start": v(388.07, 125) * mm, "end": v(416.93, 125) * mm});
            skLineSegment(sketch, "E3.7.2.23", {"start": v(390.9, 119.96) * mm, "end": v(413.99, 120.04) * mm});
            skLineSegment(sketch, "E3.7.2.28", {"start": v(373.63, 100) * mm, "end": v(388.07, 125) * mm});
            skLineSegment(sketch, "E3.7.2.31", {"start": v(416.93, 125) * mm, "end": v(431.37, 100) * mm});
            skCircle(sketch, "E3.7.2.36", {"center": v(402.5, 100) * mm, "radius": 20 * mm, "construction": true});
            skLineSegment(sketch, "E3.7.2.38", {"start": v(379.4, 99.93) * mm, "end": v(390.9, 119.96) * mm});
            skLineSegment(sketch, "E3.7.2.39", {"start": v(391.01, 79.96) * mm, "end": v(379.4, 99.93) * mm});
            skLineSegment(sketch, "E3.7.2.40", {"start": v(425.6, 100.07) * mm, "end": v(414.1, 80.04) * mm});
            skLineSegment(sketch, "E3.7.2.41", {"start": v(413.99, 120.04) * mm, "end": v(425.6, 100.07) * mm});
            skLineSegment(sketch, "E3.7.3.7", {"start": v(388.07, 125) * mm, "end": v(373.63, 150) * mm});
            skLineSegment(sketch, "E3.7.3.9", {"start": v(416.93, 125) * mm, "end": v(388.07, 125) * mm});
            skLineSegment(sketch, "E3.7.3.10", {"start": v(431.37, 150) * mm, "end": v(416.93, 125) * mm});
            skPoint(sketch, "E3.7.3.12", {"position": v(402.5, 175) * mm});
            skPoint(sketch, "E3.7.3.13", {"position": v(419.79, 160.05) * mm});
            skLineSegment(sketch, "E3.7.3.16", {"start": v(414.1, 130.04) * mm, "end": v(391.01, 129.96) * mm});
            skCircle(sketch, "E3.7.3.19", {"center": v(402.5, 150) * mm, "radius": 25 * mm, "construction": true});
            skLineSegment(sketch, "E3.7.3.20", {"start": v(388.07, 175) * mm, "end": v(416.93, 175) * mm});
            skLineSegment(sketch, "E3.7.3.23", {"start": v(390.9, 169.96) * mm, "end": v(413.99, 170.04) * mm});
            skLineSegment(sketch, "E3.7.3.28", {"start": v(373.63, 150) * mm, "end": v(388.07, 175) * mm});
            skLineSegment(sketch, "E3.7.3.31", {"start": v(416.93, 175) * mm, "end": v(431.37, 150) * mm});
            skCircle(sketch, "E3.7.3.36", {"center": v(402.5, 150) * mm, "radius": 20 * mm, "construction": true});
            skLineSegment(sketch, "E3.7.3.38", {"start": v(379.4, 149.93) * mm, "end": v(390.9, 169.96) * mm});
            skLineSegment(sketch, "E3.7.3.39", {"start": v(391.01, 129.96) * mm, "end": v(379.4, 149.93) * mm});
            skLineSegment(sketch, "E3.7.3.40", {"start": v(425.6, 150.07) * mm, "end": v(414.1, 130.04) * mm});
            skLineSegment(sketch, "E3.7.3.41", {"start": v(413.99, 170.04) * mm, "end": v(425.6, 150.07) * mm});
            skLineSegment(sketch, "E3.7.4.7", {"start": v(388.07, 175) * mm, "end": v(373.63, 200) * mm});
            skLineSegment(sketch, "E3.7.4.9", {"start": v(416.93, 175) * mm, "end": v(388.07, 175) * mm});
            skLineSegment(sketch, "E3.7.4.10", {"start": v(431.37, 200) * mm, "end": v(416.93, 175) * mm});
            skPoint(sketch, "E3.7.4.12", {"position": v(402.5, 225) * mm});
            skPoint(sketch, "E3.7.4.13", {"position": v(419.79, 210.05) * mm});
            skLineSegment(sketch, "E3.7.4.16", {"start": v(414.1, 180.04) * mm, "end": v(391.01, 179.96) * mm});
            skCircle(sketch, "E3.7.4.19", {"center": v(402.5, 200) * mm, "radius": 25 * mm, "construction": true});
            skLineSegment(sketch, "E3.7.4.20", {"start": v(388.07, 225) * mm, "end": v(416.93, 225) * mm});
            skLineSegment(sketch, "E3.7.4.23", {"start": v(390.9, 219.96) * mm, "end": v(413.99, 220.04) * mm});
            skLineSegment(sketch, "E3.7.4.28", {"start": v(373.63, 200) * mm, "end": v(388.07, 225) * mm});
            skLineSegment(sketch, "E3.7.4.31", {"start": v(416.93, 225) * mm, "end": v(431.37, 200) * mm});
            skCircle(sketch, "E3.7.4.36", {"center": v(402.5, 200) * mm, "radius": 20 * mm, "construction": true});
            skLineSegment(sketch, "E3.7.4.38", {"start": v(379.4, 199.93) * mm, "end": v(390.9, 219.96) * mm});
            skLineSegment(sketch, "E3.7.4.39", {"start": v(391.01, 179.96) * mm, "end": v(379.4, 199.93) * mm});
            skLineSegment(sketch, "E3.7.4.40", {"start": v(425.6, 200.07) * mm, "end": v(414.1, 180.04) * mm});
            skLineSegment(sketch, "E3.7.4.41", {"start": v(413.99, 220.04) * mm, "end": v(425.6, 200.07) * mm});
            skLineSegment(sketch, "E3.7.5.7", {"start": v(388.07, 225) * mm, "end": v(373.63, 250) * mm});
            skLineSegment(sketch, "E3.7.5.9", {"start": v(416.93, 225) * mm, "end": v(388.07, 225) * mm});
            skLineSegment(sketch, "E3.7.5.10", {"start": v(431.37, 250) * mm, "end": v(416.93, 225) * mm});
            skPoint(sketch, "E3.7.5.12", {"position": v(402.5, 275) * mm});
            skPoint(sketch, "E3.7.5.13", {"position": v(419.79, 260.05) * mm});
            skLineSegment(sketch, "E3.7.5.16", {"start": v(414.1, 230.04) * mm, "end": v(391.01, 229.96) * mm});
            skCircle(sketch, "E3.7.5.19", {"center": v(402.5, 250) * mm, "radius": 25 * mm, "construction": true});
            skLineSegment(sketch, "E3.7.5.20", {"start": v(388.07, 275) * mm, "end": v(416.93, 275) * mm});
            skLineSegment(sketch, "E3.7.5.23", {"start": v(390.9, 269.96) * mm, "end": v(413.99, 270.04) * mm});
            skLineSegment(sketch, "E3.7.5.28", {"start": v(373.63, 250) * mm, "end": v(388.07, 275) * mm});
            skLineSegment(sketch, "E3.7.5.31", {"start": v(416.93, 275) * mm, "end": v(431.37, 250) * mm});
            skCircle(sketch, "E3.7.5.36", {"center": v(402.5, 250) * mm, "radius": 20 * mm, "construction": true});
            skLineSegment(sketch, "E3.7.5.38", {"start": v(379.4, 249.93) * mm, "end": v(390.9, 269.96) * mm});
            skLineSegment(sketch, "E3.7.5.39", {"start": v(391.01, 229.96) * mm, "end": v(379.4, 249.93) * mm});
            skLineSegment(sketch, "E3.7.5.40", {"start": v(425.6, 250.07) * mm, "end": v(414.1, 230.04) * mm});
            skLineSegment(sketch, "E3.7.5.41", {"start": v(413.99, 270.04) * mm, "end": v(425.6, 250.07) * mm});
            skLineSegment(sketch, "E3.7.6.7", {"start": v(388.07, 275) * mm, "end": v(373.63, 300) * mm});
            skLineSegment(sketch, "E3.7.6.9", {"start": v(416.93, 275) * mm, "end": v(388.07, 275) * mm});
            skLineSegment(sketch, "E3.7.6.10", {"start": v(431.37, 300) * mm, "end": v(416.93, 275) * mm});
            skPoint(sketch, "E3.7.6.12", {"position": v(402.5, 325) * mm});
            skPoint(sketch, "E3.7.6.13", {"position": v(419.79, 310.05) * mm});
            skLineSegment(sketch, "E3.7.6.16", {"start": v(414.1, 280.04) * mm, "end": v(391.01, 279.96) * mm});
            skCircle(sketch, "E3.7.6.19", {"center": v(402.5, 300) * mm, "radius": 25 * mm, "construction": true});
            skLineSegment(sketch, "E3.7.6.20", {"start": v(388.07, 325) * mm, "end": v(416.93, 325) * mm});
            skLineSegment(sketch, "E3.7.6.23", {"start": v(390.9, 319.96) * mm, "end": v(413.99, 320.04) * mm});
            skLineSegment(sketch, "E3.7.6.28", {"start": v(373.63, 300) * mm, "end": v(388.07, 325) * mm});
            skLineSegment(sketch, "E3.7.6.31", {"start": v(416.93, 325) * mm, "end": v(431.37, 300) * mm});
            skCircle(sketch, "E3.7.6.36", {"center": v(402.5, 300) * mm, "radius": 20 * mm, "construction": true});
            skLineSegment(sketch, "E3.7.6.38", {"start": v(379.4, 299.93) * mm, "end": v(390.9, 319.96) * mm});
            skLineSegment(sketch, "E3.7.6.39", {"start": v(391.01, 279.96) * mm, "end": v(379.4, 299.93) * mm});
            skLineSegment(sketch, "E3.7.6.40", {"start": v(425.6, 300.07) * mm, "end": v(414.1, 280.04) * mm});
            skLineSegment(sketch, "E3.7.6.41", {"start": v(413.99, 320.04) * mm, "end": v(425.6, 300.07) * mm});
            skLineSegment(sketch, "E3.7.7.7", {"start": v(388.07, 325) * mm, "end": v(373.63, 350) * mm});
            skLineSegment(sketch, "E3.7.7.9", {"start": v(416.93, 325) * mm, "end": v(388.07, 325) * mm});
            skLineSegment(sketch, "E3.7.7.10", {"start": v(431.37, 350) * mm, "end": v(416.93, 325) * mm});
            skPoint(sketch, "E3.7.7.12", {"position": v(402.5, 375) * mm});
            skPoint(sketch, "E3.7.7.13", {"position": v(419.79, 360.05) * mm});
            skLineSegment(sketch, "E3.7.7.16", {"start": v(414.1, 330.04) * mm, "end": v(391.01, 329.96) * mm});
            skCircle(sketch, "E3.7.7.19", {"center": v(402.5, 350) * mm, "radius": 25 * mm, "construction": true});
            skLineSegment(sketch, "E3.7.7.20", {"start": v(388.07, 375) * mm, "end": v(416.93, 375) * mm});
            skLineSegment(sketch, "E3.7.7.23", {"start": v(390.9, 369.96) * mm, "end": v(413.99, 370.04) * mm});
            skLineSegment(sketch, "E3.7.7.28", {"start": v(373.63, 350) * mm, "end": v(388.07, 375) * mm});
            skLineSegment(sketch, "E3.7.7.31", {"start": v(416.93, 375) * mm, "end": v(431.37, 350) * mm});
            skCircle(sketch, "E3.7.7.36", {"center": v(402.5, 350) * mm, "radius": 20 * mm, "construction": true});
            skLineSegment(sketch, "E3.7.7.38", {"start": v(379.4, 349.93) * mm, "end": v(390.9, 369.96) * mm});
            skLineSegment(sketch, "E3.7.7.39", {"start": v(391.01, 329.96) * mm, "end": v(379.4, 349.93) * mm});
            skLineSegment(sketch, "E3.7.7.40", {"start": v(425.6, 350.07) * mm, "end": v(414.1, 330.04) * mm});
            skLineSegment(sketch, "E3.7.7.41", {"start": v(413.99, 370.04) * mm, "end": v(425.6, 350.07) * mm});
            skLineSegment(sketch, "E3.7.8.7", {"start": v(388.07, 375) * mm, "end": v(373.63, 400) * mm});
            skLineSegment(sketch, "E3.7.8.9", {"start": v(416.93, 375) * mm, "end": v(388.07, 375) * mm});
            skLineSegment(sketch, "E3.7.8.10", {"start": v(431.37, 400) * mm, "end": v(416.93, 375) * mm});
            skPoint(sketch, "E3.7.8.12", {"position": v(402.5, 425) * mm});
            skPoint(sketch, "E3.7.8.13", {"position": v(419.79, 410.05) * mm});
            skLineSegment(sketch, "E3.7.8.16", {"start": v(414.1, 380.04) * mm, "end": v(391.01, 379.96) * mm});
            skCircle(sketch, "E3.7.8.19", {"center": v(402.5, 400) * mm, "radius": 25 * mm, "construction": true});
            skLineSegment(sketch, "E3.7.8.20", {"start": v(388.07, 425) * mm, "end": v(416.93, 425) * mm});
            skLineSegment(sketch, "E3.7.8.23", {"start": v(390.9, 419.96) * mm, "end": v(413.99, 420.04) * mm});
            skLineSegment(sketch, "E3.7.8.28", {"start": v(373.63, 400) * mm, "end": v(388.07, 425) * mm});
            skLineSegment(sketch, "E3.7.8.31", {"start": v(416.93, 425) * mm, "end": v(431.37, 400) * mm});
            skCircle(sketch, "E3.7.8.36", {"center": v(402.5, 400) * mm, "radius": 20 * mm, "construction": true});
            skLineSegment(sketch, "E3.7.8.38", {"start": v(379.4, 399.93) * mm, "end": v(390.9, 419.96) * mm});
            skLineSegment(sketch, "E3.7.8.39", {"start": v(391.01, 379.96) * mm, "end": v(379.4, 399.93) * mm});
            skLineSegment(sketch, "E3.7.8.40", {"start": v(425.6, 400.07) * mm, "end": v(414.1, 380.04) * mm});
            skLineSegment(sketch, "E3.7.8.41", {"start": v(413.99, 420.04) * mm, "end": v(425.6, 400.07) * mm});
            skLineSegment(sketch, "E3.7.9.7", {"start": v(388.07, 425) * mm, "end": v(373.63, 450) * mm});
            skLineSegment(sketch, "E3.7.9.9", {"start": v(416.93, 425) * mm, "end": v(388.07, 425) * mm});
            skLineSegment(sketch, "E3.7.9.10", {"start": v(431.37, 450) * mm, "end": v(416.93, 425) * mm});
            skPoint(sketch, "E3.7.9.12", {"position": v(402.5, 475) * mm});
            skPoint(sketch, "E3.7.9.13", {"position": v(419.79, 460.05) * mm});
            skLineSegment(sketch, "E3.7.9.16", {"start": v(414.1, 430.04) * mm, "end": v(391.01, 429.96) * mm});
            skCircle(sketch, "E3.7.9.19", {"center": v(402.5, 450) * mm, "radius": 25 * mm, "construction": true});
            skLineSegment(sketch, "E3.7.9.20", {"start": v(388.07, 475) * mm, "end": v(416.93, 475) * mm});
            skLineSegment(sketch, "E3.7.9.23", {"start": v(390.9, 469.96) * mm, "end": v(413.99, 470.04) * mm});
            skLineSegment(sketch, "E3.7.9.28", {"start": v(373.63, 450) * mm, "end": v(388.07, 475) * mm});
            skLineSegment(sketch, "E3.7.9.31", {"start": v(416.93, 475) * mm, "end": v(431.37, 450) * mm});
            skCircle(sketch, "E3.7.9.36", {"center": v(402.5, 450) * mm, "radius": 20 * mm, "construction": true});
            skLineSegment(sketch, "E3.7.9.38", {"start": v(379.4, 449.93) * mm, "end": v(390.9, 469.96) * mm});
            skLineSegment(sketch, "E3.7.9.39", {"start": v(391.01, 429.96) * mm, "end": v(379.4, 449.93) * mm});
            skLineSegment(sketch, "E3.7.9.40", {"start": v(425.6, 450.07) * mm, "end": v(414.1, 430.04) * mm});
            skLineSegment(sketch, "E3.7.9.41", {"start": v(413.99, 470.04) * mm, "end": v(425.6, 450.07) * mm});
            skLineSegment(sketch, "E3.8.0.7", {"start": v(445.57, -25) * mm, "end": v(431.13, 0) * mm});
            skLineSegment(sketch, "E3.8.0.9", {"start": v(474.43, -25) * mm, "end": v(445.57, -25) * mm});
            skLineSegment(sketch, "E3.8.0.10", {"start": v(488.87, 0) * mm, "end": v(474.43, -25) * mm});
            skPoint(sketch, "E3.8.0.12", {"position": v(460, 25) * mm});
            skPoint(sketch, "E3.8.0.13", {"position": v(477.29, 10.05) * mm});
            skLineSegment(sketch, "E3.8.0.16", {"start": v(471.6, -19.96) * mm, "end": v(448.51, -20.04) * mm});
            skCircle(sketch, "E3.8.0.19", {"center": v(460, 0) * mm, "radius": 25 * mm, "construction": true});
            skLineSegment(sketch, "E3.8.0.20", {"start": v(445.57, 25) * mm, "end": v(474.43, 25) * mm});
            skLineSegment(sketch, "E3.8.0.23", {"start": v(448.4, 19.96) * mm, "end": v(471.49, 20.04) * mm});
            skLineSegment(sketch, "E3.8.0.28", {"start": v(431.13, 0) * mm, "end": v(445.57, 25) * mm});
            skLineSegment(sketch, "E3.8.0.31", {"start": v(474.43, 25) * mm, "end": v(488.87, 0) * mm});
            skCircle(sketch, "E3.8.0.36", {"center": v(460, 0) * mm, "radius": 20 * mm, "construction": true});
            skLineSegment(sketch, "E3.8.0.38", {"start": v(436.9, -0.07) * mm, "end": v(448.4, 19.96) * mm});
            skLineSegment(sketch, "E3.8.0.39", {"start": v(448.51, -20.04) * mm, "end": v(436.9, -0.07) * mm});
            skLineSegment(sketch, "E3.8.0.40", {"start": v(483.1, 0.07) * mm, "end": v(471.6, -19.96) * mm});
            skLineSegment(sketch, "E3.8.0.41", {"start": v(471.49, 20.04) * mm, "end": v(483.1, 0.07) * mm});
            skLineSegment(sketch, "E3.8.1.7", {"start": v(445.57, 25) * mm, "end": v(431.13, 50) * mm});
            skLineSegment(sketch, "E3.8.1.9", {"start": v(474.43, 25) * mm, "end": v(445.57, 25) * mm});
            skLineSegment(sketch, "E3.8.1.10", {"start": v(488.87, 50) * mm, "end": v(474.43, 25) * mm});
            skPoint(sketch, "E3.8.1.12", {"position": v(460, 75) * mm});
            skPoint(sketch, "E3.8.1.13", {"position": v(477.29, 60.05) * mm});
            skLineSegment(sketch, "E3.8.1.16", {"start": v(471.6, 30.04) * mm, "end": v(448.51, 29.96) * mm});
            skCircle(sketch, "E3.8.1.19", {"center": v(460, 50) * mm, "radius": 25 * mm, "construction": true});
            skLineSegment(sketch, "E3.8.1.20", {"start": v(445.57, 75) * mm, "end": v(474.43, 75) * mm});
            skLineSegment(sketch, "E3.8.1.23", {"start": v(448.4, 69.96) * mm, "end": v(471.49, 70.04) * mm});
            skLineSegment(sketch, "E3.8.1.28", {"start": v(431.13, 50) * mm, "end": v(445.57, 75) * mm});
            skLineSegment(sketch, "E3.8.1.31", {"start": v(474.43, 75) * mm, "end": v(488.87, 50) * mm});
            skCircle(sketch, "E3.8.1.36", {"center": v(460, 50) * mm, "radius": 20 * mm, "construction": true});
            skLineSegment(sketch, "E3.8.1.38", {"start": v(436.9, 49.93) * mm, "end": v(448.4, 69.96) * mm});
            skLineSegment(sketch, "E3.8.1.39", {"start": v(448.51, 29.96) * mm, "end": v(436.9, 49.93) * mm});
            skLineSegment(sketch, "E3.8.1.40", {"start": v(483.1, 50.07) * mm, "end": v(471.6, 30.04) * mm});
            skLineSegment(sketch, "E3.8.1.41", {"start": v(471.49, 70.04) * mm, "end": v(483.1, 50.07) * mm});
            skLineSegment(sketch, "E3.8.2.7", {"start": v(445.57, 75) * mm, "end": v(431.13, 100) * mm});
            skLineSegment(sketch, "E3.8.2.9", {"start": v(474.43, 75) * mm, "end": v(445.57, 75) * mm});
            skLineSegment(sketch, "E3.8.2.10", {"start": v(488.87, 100) * mm, "end": v(474.43, 75) * mm});
            skPoint(sketch, "E3.8.2.12", {"position": v(460, 125) * mm});
            skPoint(sketch, "E3.8.2.13", {"position": v(477.29, 110.05) * mm});
            skLineSegment(sketch, "E3.8.2.16", {"start": v(471.6, 80.04) * mm, "end": v(448.51, 79.96) * mm});
            skCircle(sketch, "E3.8.2.19", {"center": v(460, 100) * mm, "radius": 25 * mm, "construction": true});
            skLineSegment(sketch, "E3.8.2.20", {"start": v(445.57, 125) * mm, "end": v(474.43, 125) * mm});
            skLineSegment(sketch, "E3.8.2.23", {"start": v(448.4, 119.96) * mm, "end": v(471.49, 120.04) * mm});
            skLineSegment(sketch, "E3.8.2.28", {"start": v(431.13, 100) * mm, "end": v(445.57, 125) * mm});
            skLineSegment(sketch, "E3.8.2.31", {"start": v(474.43, 125) * mm, "end": v(488.87, 100) * mm});
            skCircle(sketch, "E3.8.2.36", {"center": v(460, 100) * mm, "radius": 20 * mm, "construction": true});
            skLineSegment(sketch, "E3.8.2.38", {"start": v(436.9, 99.93) * mm, "end": v(448.4, 119.96) * mm});
            skLineSegment(sketch, "E3.8.2.39", {"start": v(448.51, 79.96) * mm, "end": v(436.9, 99.93) * mm});
            skLineSegment(sketch, "E3.8.2.40", {"start": v(483.1, 100.07) * mm, "end": v(471.6, 80.04) * mm});
            skLineSegment(sketch, "E3.8.2.41", {"start": v(471.49, 120.04) * mm, "end": v(483.1, 100.07) * mm});
            skLineSegment(sketch, "E3.8.3.7", {"start": v(445.57, 125) * mm, "end": v(431.13, 150) * mm});
            skLineSegment(sketch, "E3.8.3.9", {"start": v(474.43, 125) * mm, "end": v(445.57, 125) * mm});
            skLineSegment(sketch, "E3.8.3.10", {"start": v(488.87, 150) * mm, "end": v(474.43, 125) * mm});
            skPoint(sketch, "E3.8.3.12", {"position": v(460, 175) * mm});
            skPoint(sketch, "E3.8.3.13", {"position": v(477.29, 160.05) * mm});
            skLineSegment(sketch, "E3.8.3.16", {"start": v(471.6, 130.04) * mm, "end": v(448.51, 129.96) * mm});
            skCircle(sketch, "E3.8.3.19", {"center": v(460, 150) * mm, "radius": 25 * mm, "construction": true});
            skLineSegment(sketch, "E3.8.3.20", {"start": v(445.57, 175) * mm, "end": v(474.43, 175) * mm});
            skLineSegment(sketch, "E3.8.3.23", {"start": v(448.4, 169.96) * mm, "end": v(471.49, 170.04) * mm});
            skLineSegment(sketch, "E3.8.3.28", {"start": v(431.13, 150) * mm, "end": v(445.57, 175) * mm});
            skLineSegment(sketch, "E3.8.3.31", {"start": v(474.43, 175) * mm, "end": v(488.87, 150) * mm});
            skCircle(sketch, "E3.8.3.36", {"center": v(460, 150) * mm, "radius": 20 * mm, "construction": true});
            skLineSegment(sketch, "E3.8.3.38", {"start": v(436.9, 149.93) * mm, "end": v(448.4, 169.96) * mm});
            skLineSegment(sketch, "E3.8.3.39", {"start": v(448.51, 129.96) * mm, "end": v(436.9, 149.93) * mm});
            skLineSegment(sketch, "E3.8.3.40", {"start": v(483.1, 150.07) * mm, "end": v(471.6, 130.04) * mm});
            skLineSegment(sketch, "E3.8.3.41", {"start": v(471.49, 170.04) * mm, "end": v(483.1, 150.07) * mm});
            skLineSegment(sketch, "E3.8.4.7", {"start": v(445.57, 175) * mm, "end": v(431.13, 200) * mm});
            skLineSegment(sketch, "E3.8.4.9", {"start": v(474.43, 175) * mm, "end": v(445.57, 175) * mm});
            skLineSegment(sketch, "E3.8.4.10", {"start": v(488.87, 200) * mm, "end": v(474.43, 175) * mm});
            skPoint(sketch, "E3.8.4.12", {"position": v(460, 225) * mm});
            skPoint(sketch, "E3.8.4.13", {"position": v(477.29, 210.05) * mm});
            skLineSegment(sketch, "E3.8.4.16", {"start": v(471.6, 180.04) * mm, "end": v(448.51, 179.96) * mm});
            skCircle(sketch, "E3.8.4.19", {"center": v(460, 200) * mm, "radius": 25 * mm, "construction": true});
            skLineSegment(sketch, "E3.8.4.20", {"start": v(445.57, 225) * mm, "end": v(474.43, 225) * mm});
            skLineSegment(sketch, "E3.8.4.23", {"start": v(448.4, 219.96) * mm, "end": v(471.49, 220.04) * mm});
            skLineSegment(sketch, "E3.8.4.28", {"start": v(431.13, 200) * mm, "end": v(445.57, 225) * mm});
            skLineSegment(sketch, "E3.8.4.31", {"start": v(474.43, 225) * mm, "end": v(488.87, 200) * mm});
            skCircle(sketch, "E3.8.4.36", {"center": v(460, 200) * mm, "radius": 20 * mm, "construction": true});
            skLineSegment(sketch, "E3.8.4.38", {"start": v(436.9, 199.93) * mm, "end": v(448.4, 219.96) * mm});
            skLineSegment(sketch, "E3.8.4.39", {"start": v(448.51, 179.96) * mm, "end": v(436.9, 199.93) * mm});
            skLineSegment(sketch, "E3.8.4.40", {"start": v(483.1, 200.07) * mm, "end": v(471.6, 180.04) * mm});
            skLineSegment(sketch, "E3.8.4.41", {"start": v(471.49, 220.04) * mm, "end": v(483.1, 200.07) * mm});
            skLineSegment(sketch, "E3.8.5.7", {"start": v(445.57, 225) * mm, "end": v(431.13, 250) * mm});
            skLineSegment(sketch, "E3.8.5.9", {"start": v(474.43, 225) * mm, "end": v(445.57, 225) * mm});
            skLineSegment(sketch, "E3.8.5.10", {"start": v(488.87, 250) * mm, "end": v(474.43, 225) * mm});
            skPoint(sketch, "E3.8.5.12", {"position": v(460, 275) * mm});
            skPoint(sketch, "E3.8.5.13", {"position": v(477.29, 260.05) * mm});
            skLineSegment(sketch, "E3.8.5.16", {"start": v(471.6, 230.04) * mm, "end": v(448.51, 229.96) * mm});
            skCircle(sketch, "E3.8.5.19", {"center": v(460, 250) * mm, "radius": 25 * mm, "construction": true});
            skLineSegment(sketch, "E3.8.5.20", {"start": v(445.57, 275) * mm, "end": v(474.43, 275) * mm});
            skLineSegment(sketch, "E3.8.5.23", {"start": v(448.4, 269.96) * mm, "end": v(471.49, 270.04) * mm});
            skLineSegment(sketch, "E3.8.5.28", {"start": v(431.13, 250) * mm, "end": v(445.57, 275) * mm});
            skLineSegment(sketch, "E3.8.5.31", {"start": v(474.43, 275) * mm, "end": v(488.87, 250) * mm});
            skCircle(sketch, "E3.8.5.36", {"center": v(460, 250) * mm, "radius": 20 * mm, "construction": true});
            skLineSegment(sketch, "E3.8.5.38", {"start": v(436.9, 249.93) * mm, "end": v(448.4, 269.96) * mm});
            skLineSegment(sketch, "E3.8.5.39", {"start": v(448.51, 229.96) * mm, "end": v(436.9, 249.93) * mm});
            skLineSegment(sketch, "E3.8.5.40", {"start": v(483.1, 250.07) * mm, "end": v(471.6, 230.04) * mm});
            skLineSegment(sketch, "E3.8.5.41", {"start": v(471.49, 270.04) * mm, "end": v(483.1, 250.07) * mm});
            skLineSegment(sketch, "E3.8.6.7", {"start": v(445.57, 275) * mm, "end": v(431.13, 300) * mm});
            skLineSegment(sketch, "E3.8.6.9", {"start": v(474.43, 275) * mm, "end": v(445.57, 275) * mm});
            skLineSegment(sketch, "E3.8.6.10", {"start": v(488.87, 300) * mm, "end": v(474.43, 275) * mm});
            skPoint(sketch, "E3.8.6.12", {"position": v(460, 325) * mm});
            skPoint(sketch, "E3.8.6.13", {"position": v(477.29, 310.05) * mm});
            skLineSegment(sketch, "E3.8.6.16", {"start": v(471.6, 280.04) * mm, "end": v(448.51, 279.96) * mm});
            skCircle(sketch, "E3.8.6.19", {"center": v(460, 300) * mm, "radius": 25 * mm, "construction": true});
            skLineSegment(sketch, "E3.8.6.20", {"start": v(445.57, 325) * mm, "end": v(474.43, 325) * mm});
            skLineSegment(sketch, "E3.8.6.23", {"start": v(448.4, 319.96) * mm, "end": v(471.49, 320.04) * mm});
            skLineSegment(sketch, "E3.8.6.28", {"start": v(431.13, 300) * mm, "end": v(445.57, 325) * mm});
            skLineSegment(sketch, "E3.8.6.31", {"start": v(474.43, 325) * mm, "end": v(488.87, 300) * mm});
            skCircle(sketch, "E3.8.6.36", {"center": v(460, 300) * mm, "radius": 20 * mm, "construction": true});
            skLineSegment(sketch, "E3.8.6.38", {"start": v(436.9, 299.93) * mm, "end": v(448.4, 319.96) * mm});
            skLineSegment(sketch, "E3.8.6.39", {"start": v(448.51, 279.96) * mm, "end": v(436.9, 299.93) * mm});
            skLineSegment(sketch, "E3.8.6.40", {"start": v(483.1, 300.07) * mm, "end": v(471.6, 280.04) * mm});
            skLineSegment(sketch, "E3.8.6.41", {"start": v(471.49, 320.04) * mm, "end": v(483.1, 300.07) * mm});
            skLineSegment(sketch, "E3.8.7.7", {"start": v(445.57, 325) * mm, "end": v(431.13, 350) * mm});
            skLineSegment(sketch, "E3.8.7.9", {"start": v(474.43, 325) * mm, "end": v(445.57, 325) * mm});
            skLineSegment(sketch, "E3.8.7.10", {"start": v(488.87, 350) * mm, "end": v(474.43, 325) * mm});
            skPoint(sketch, "E3.8.7.12", {"position": v(460, 375) * mm});
            skPoint(sketch, "E3.8.7.13", {"position": v(477.29, 360.05) * mm});
            skLineSegment(sketch, "E3.8.7.16", {"start": v(471.6, 330.04) * mm, "end": v(448.51, 329.96) * mm});
            skCircle(sketch, "E3.8.7.19", {"center": v(460, 350) * mm, "radius": 25 * mm, "construction": true});
            skLineSegment(sketch, "E3.8.7.20", {"start": v(445.57, 375) * mm, "end": v(474.43, 375) * mm});
            skLineSegment(sketch, "E3.8.7.23", {"start": v(448.4, 369.96) * mm, "end": v(471.49, 370.04) * mm});
            skLineSegment(sketch, "E3.8.7.28", {"start": v(431.13, 350) * mm, "end": v(445.57, 375) * mm});
            skLineSegment(sketch, "E3.8.7.31", {"start": v(474.43, 375) * mm, "end": v(488.87, 350) * mm});
            skCircle(sketch, "E3.8.7.36", {"center": v(460, 350) * mm, "radius": 20 * mm, "construction": true});
            skLineSegment(sketch, "E3.8.7.38", {"start": v(436.9, 349.93) * mm, "end": v(448.4, 369.96) * mm});
            skLineSegment(sketch, "E3.8.7.39", {"start": v(448.51, 329.96) * mm, "end": v(436.9, 349.93) * mm});
            skLineSegment(sketch, "E3.8.7.40", {"start": v(483.1, 350.07) * mm, "end": v(471.6, 330.04) * mm});
            skLineSegment(sketch, "E3.8.7.41", {"start": v(471.49, 370.04) * mm, "end": v(483.1, 350.07) * mm});
            skLineSegment(sketch, "E3.8.8.7", {"start": v(445.57, 375) * mm, "end": v(431.13, 400) * mm});
            skLineSegment(sketch, "E3.8.8.9", {"start": v(474.43, 375) * mm, "end": v(445.57, 375) * mm});
            skLineSegment(sketch, "E3.8.8.10", {"start": v(488.87, 400) * mm, "end": v(474.43, 375) * mm});
            skPoint(sketch, "E3.8.8.12", {"position": v(460, 425) * mm});
            skPoint(sketch, "E3.8.8.13", {"position": v(477.29, 410.05) * mm});
            skLineSegment(sketch, "E3.8.8.16", {"start": v(471.6, 380.04) * mm, "end": v(448.51, 379.96) * mm});
            skCircle(sketch, "E3.8.8.19", {"center": v(460, 400) * mm, "radius": 25 * mm, "construction": true});
            skLineSegment(sketch, "E3.8.8.20", {"start": v(445.57, 425) * mm, "end": v(474.43, 425) * mm});
            skLineSegment(sketch, "E3.8.8.23", {"start": v(448.4, 419.96) * mm, "end": v(471.49, 420.04) * mm});
            skLineSegment(sketch, "E3.8.8.28", {"start": v(431.13, 400) * mm, "end": v(445.57, 425) * mm});
            skLineSegment(sketch, "E3.8.8.31", {"start": v(474.43, 425) * mm, "end": v(488.87, 400) * mm});
            skCircle(sketch, "E3.8.8.36", {"center": v(460, 400) * mm, "radius": 20 * mm, "construction": true});
            skLineSegment(sketch, "E3.8.8.38", {"start": v(436.9, 399.93) * mm, "end": v(448.4, 419.96) * mm});
            skLineSegment(sketch, "E3.8.8.39", {"start": v(448.51, 379.96) * mm, "end": v(436.9, 399.93) * mm});
            skLineSegment(sketch, "E3.8.8.40", {"start": v(483.1, 400.07) * mm, "end": v(471.6, 380.04) * mm});
            skLineSegment(sketch, "E3.8.8.41", {"start": v(471.49, 420.04) * mm, "end": v(483.1, 400.07) * mm});
            skLineSegment(sketch, "E3.8.9.7", {"start": v(445.57, 425) * mm, "end": v(431.13, 450) * mm});
            skLineSegment(sketch, "E3.8.9.9", {"start": v(474.43, 425) * mm, "end": v(445.57, 425) * mm});
            skLineSegment(sketch, "E3.8.9.10", {"start": v(488.87, 450) * mm, "end": v(474.43, 425) * mm});
            skPoint(sketch, "E3.8.9.12", {"position": v(460, 475) * mm});
            skPoint(sketch, "E3.8.9.13", {"position": v(477.29, 460.05) * mm});
            skLineSegment(sketch, "E3.8.9.16", {"start": v(471.6, 430.04) * mm, "end": v(448.51, 429.96) * mm});
            skCircle(sketch, "E3.8.9.19", {"center": v(460, 450) * mm, "radius": 25 * mm, "construction": true});
            skLineSegment(sketch, "E3.8.9.20", {"start": v(445.57, 475) * mm, "end": v(474.43, 475) * mm});
            skLineSegment(sketch, "E3.8.9.23", {"start": v(448.4, 469.96) * mm, "end": v(471.49, 470.04) * mm});
            skLineSegment(sketch, "E3.8.9.28", {"start": v(431.13, 450) * mm, "end": v(445.57, 475) * mm});
            skLineSegment(sketch, "E3.8.9.31", {"start": v(474.43, 475) * mm, "end": v(488.87, 450) * mm});
            skCircle(sketch, "E3.8.9.36", {"center": v(460, 450) * mm, "radius": 20 * mm, "construction": true});
            skLineSegment(sketch, "E3.8.9.38", {"start": v(436.9, 449.93) * mm, "end": v(448.4, 469.96) * mm});
            skLineSegment(sketch, "E3.8.9.39", {"start": v(448.51, 429.96) * mm, "end": v(436.9, 449.93) * mm});
            skLineSegment(sketch, "E3.8.9.40", {"start": v(483.1, 450.07) * mm, "end": v(471.6, 430.04) * mm});
            skLineSegment(sketch, "E3.8.9.41", {"start": v(471.49, 470.04) * mm, "end": v(483.1, 450.07) * mm});
            skLineSegment(sketch, "E3.direction1", {"start": v(23.1, 0.07) * mm, "end": v(80.6, 0.07) * mm, "construction": true});
            skLineSegment(sketch, "E3.direction2", {"start": v(23.1, 0.07) * mm, "end": v(23.1, 50.07) * mm, "construction": true});
            skSolve(sketch);
        }
        {
            var Q0;
            {var subQ8=sQuery(id+"F2.wireOp",EDGE,"E1.3");Q0=makeQuery(id+"F2.imprint","IMPRINT",FACE,{"disambiguationData":[TD([[makeQuery(id+"F2.imprint","IMPRINT",EDGE,{"derivedFrom":subQ8}),-1.0]])]});}
            var Q1;
            {var subQ11=sQuery(id+"F2.wireOp",EDGE,"E3.1.0.9");Q1=makeQuery(id+"F2.imprint","IMPRINT",FACE,{"disambiguationData":[TD([[makeQuery(id+"F2.imprint","IMPRINT",EDGE,{"derivedFrom":subQ11}),-1.0]])]});}
            var Q2;
            {var subQ11=sQuery(id+"F2.wireOp",EDGE,"E3.2.0.9");Q2=makeQuery(id+"F2.imprint","IMPRINT",FACE,{"disambiguationData":[TD([[makeQuery(id+"F2.imprint","IMPRINT",EDGE,{"derivedFrom":subQ11}),-1.0]])]});}
            var Q3;
            {var subQ11=sQuery(id+"F2.wireOp",EDGE,"E3.2.1.9");Q3=makeQuery(id+"F2.imprint","IMPRINT",FACE,{"disambiguationData":[TD([[makeQuery(id+"F2.imprint","IMPRINT",EDGE,{"derivedFrom":subQ11}),-1.0]])]});}
            var Q4;
            {var subQ11=sQuery(id+"F2.wireOp",EDGE,"E3.1.1.9");Q4=makeQuery(id+"F2.imprint","IMPRINT",FACE,{"disambiguationData":[TD([[makeQuery(id+"F2.imprint","IMPRINT",EDGE,{"derivedFrom":subQ11}),-1.0]])]});}
            var Q5;
            Q5=makeQuery(id+"F2.imprint","IMPRINT",FACE,{"disambiguationData":[TD([[makeQuery(id+"F2.imprint","IMPRINT",EDGE,{"derivedFrom":sQuery(id+"F2.wireOp",EDGE,"E3.0.1.7")}),-1.0]])]});
            var Q6;
            Q6=makeQuery(id+"F2.imprint","IMPRINT",FACE,{"disambiguationData":[TD([[makeQuery(id+"F2.imprint","IMPRINT",EDGE,{"derivedFrom":sQuery(id+"F2.wireOp",EDGE,"E3.0.2.7")}),-1.0]])]});
            var Q7;
            {var subQ11=sQuery(id+"F2.wireOp",EDGE,"E3.1.2.9");Q7=makeQuery(id+"F2.imprint","IMPRINT",FACE,{"disambiguationData":[TD([[makeQuery(id+"F2.imprint","IMPRINT",EDGE,{"derivedFrom":subQ11}),-1.0]])]});}
            var Q8;
            {var subQ11=sQuery(id+"F2.wireOp",EDGE,"E3.2.2.9");Q8=makeQuery(id+"F2.imprint","IMPRINT",FACE,{"disambiguationData":[TD([[makeQuery(id+"F2.imprint","IMPRINT",EDGE,{"derivedFrom":subQ11}),-1.0]])]});}
            extrude(context, id + "F3", {"entities" : qUnion([Q0, Q1, Q2, Q3, Q4, Q5, Q6, Q7, Q8]), "depth" : 50 * mm});
        }
    });
